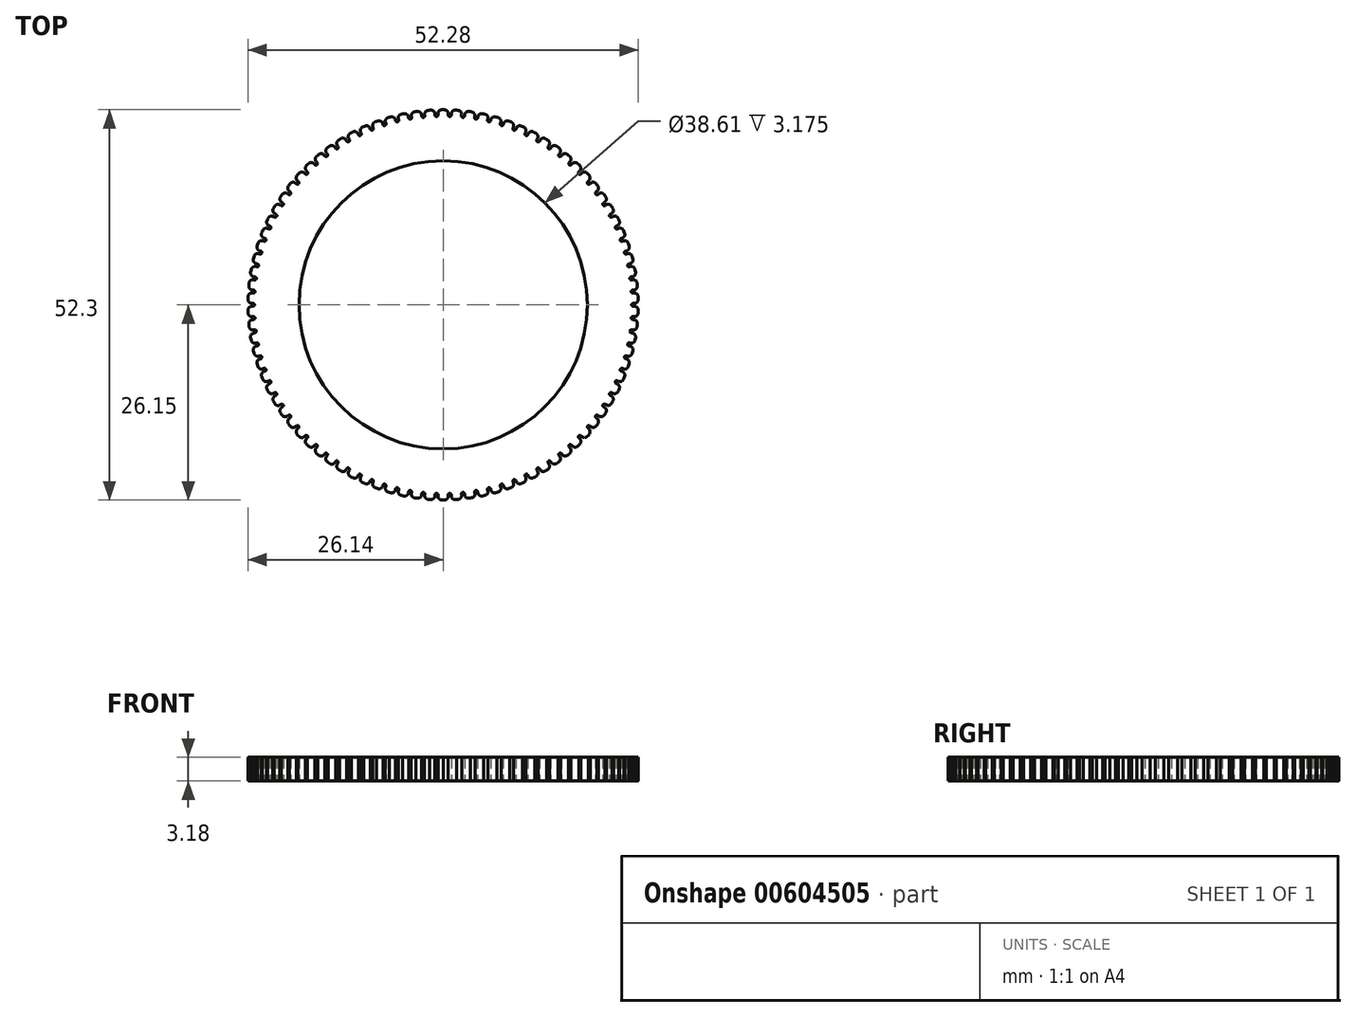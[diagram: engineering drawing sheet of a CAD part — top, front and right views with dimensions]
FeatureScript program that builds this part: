
annotation { "Feature Type Name" : "Feature", "Feature Type Description" : "" }
export const myFeature = defineFeature(function(context is Context, id is Id, definition is map)
    precondition{}
    {
        {
            var Q0;
            Q0=qCreatedBy(makeId("Top.planeOp"),FACE);
            var sketch = newSketch(context, id + "F0", { "sketchPlane" : qUnion([Q0])});
            skLineSegment(sketch, "E0", {"start": v(1.09, 25.44) * mm, "end": v(1.09, 25.44) * mm});
            skLineSegment(sketch, "E1", {"start": v(0, 0) * mm, "end": v(1.78, 25.4) * mm});
            skArc(sketch, "E2", {"start": v(0.69, 25.45) * mm, "mid": v(0.88, 25.25) * mm, "end": v(1.09, 25.44) * mm});
            skPoint(sketch, "E3.center.orphan", {"position": v(0, 25.46) * mm});
            skLineSegment(sketch, "E4", {"start": v(0.69, 25.45) * mm, "end": v(0.69, 25.45) * mm});
            skArc(sketch, "E5", {"start": v(1.82, 26.09) * mm, "mid": v(1.8, 26.09) * mm, "end": v(1.78, 26.1) * mm});
            skPoint(sketch, "E6", {"position": v(0, 26.15) * mm});
            skPoint(sketch, "E7", {"position": v(1.82, 26.09) * mm});
            skLineSegment(sketch, "E8", {"start": v(0, 26.15) * mm, "end": v(0.2, 26.15) * mm});
            skLineSegment(sketch, "E9", {"start": v(0.69, 25.45) * mm, "end": v(0.7, 25.63) * mm});
            skLineSegment(sketch, "E10", {"start": v(1.09, 25.44) * mm, "end": v(1.1, 25.6) * mm});
            skArc(sketch, "E11", {"start": v(0.7, 25.63) * mm, "mid": v(0.55, 25.99) * mm, "end": v(0.2, 26.15) * mm});
            skArc(sketch, "E12", {"start": v(1.62, 26.1) * mm, "mid": v(1.26, 25.96) * mm, "end": v(1.1, 25.6) * mm});
            skLineSegment(sketch, "E13.trimOffspring", {"start": v(1.62, 26.1) * mm, "end": v(1.82, 26.09) * mm});
            skLineSegment(sketch, "E14.1.0", {"start": v(-1.82, 26.09) * mm, "end": v(-1.62, 26.1) * mm});
            skArc(sketch, "E14.1.1", {"start": v(-1.1, 25.61) * mm, "mid": v(-1.26, 25.96) * mm, "end": v(-1.62, 26.1) * mm});
            skLineSegment(sketch, "E14.1.2", {"start": v(-1.09, 25.44) * mm, "end": v(-1.1, 25.61) * mm});
            skArc(sketch, "E14.1.3", {"start": v(-1.09, 25.44) * mm, "mid": v(-0.88, 25.25) * mm, "end": v(-0.69, 25.45) * mm});
            skLineSegment(sketch, "E14.1.4", {"start": v(-0.69, 25.45) * mm, "end": v(-0.7, 25.62) * mm});
            skArc(sketch, "E14.1.5", {"start": v(-0.2, 26.15) * mm, "mid": v(-0.56, 25.98) * mm, "end": v(-0.7, 25.62) * mm});
            skLineSegment(sketch, "E14.1.6", {"start": v(-0.2, 26.15) * mm, "end": v(0, 26.15) * mm});
            skLineSegment(sketch, "E14.2.0", {"start": v(-3.64, 25.9) * mm, "end": v(-3.44, 25.92) * mm});
            skArc(sketch, "E14.2.1", {"start": v(-2.88, 25.48) * mm, "mid": v(-3.07, 25.81) * mm, "end": v(-3.44, 25.92) * mm});
            skLineSegment(sketch, "E14.2.2", {"start": v(-2.86, 25.3) * mm, "end": v(-2.88, 25.48) * mm});
            skArc(sketch, "E14.2.3", {"start": v(-2.86, 25.3) * mm, "mid": v(-2.64, 25.13) * mm, "end": v(-2.46, 25.34) * mm});
            skLineSegment(sketch, "E14.2.4", {"start": v(-2.46, 25.34) * mm, "end": v(-2.48, 25.5) * mm});
            skArc(sketch, "E14.2.5", {"start": v(-2.03, 26.07) * mm, "mid": v(-2.37, 25.88) * mm, "end": v(-2.48, 25.5) * mm});
            skLineSegment(sketch, "E14.2.6", {"start": v(-2.03, 26.07) * mm, "end": v(-1.82, 26.09) * mm});
            skLineSegment(sketch, "E14.3.0", {"start": v(-5.44, 25.58) * mm, "end": v(-5.24, 25.62) * mm});
            skArc(sketch, "E14.3.1", {"start": v(-4.65, 25.21) * mm, "mid": v(-4.86, 25.53) * mm, "end": v(-5.24, 25.62) * mm});
            skLineSegment(sketch, "E14.3.2", {"start": v(-4.62, 25.04) * mm, "end": v(-4.65, 25.21) * mm});
            skArc(sketch, "E14.3.3", {"start": v(-4.62, 25.04) * mm, "mid": v(-4.39, 24.88) * mm, "end": v(-4.22, 25.1) * mm});
            skLineSegment(sketch, "E14.3.4", {"start": v(-4.22, 25.1) * mm, "end": v(-4.25, 25.27) * mm});
            skArc(sketch, "E14.3.5", {"start": v(-3.84, 25.86) * mm, "mid": v(-4.17, 25.65) * mm, "end": v(-4.25, 25.27) * mm});
            skLineSegment(sketch, "E14.3.6", {"start": v(-3.84, 25.86) * mm, "end": v(-3.64, 25.9) * mm});
            skLineSegment(sketch, "E14.4.0", {"start": v(-7.2, 25.14) * mm, "end": v(-7.01, 25.19) * mm});
            skArc(sketch, "E14.4.1", {"start": v(-6.4, 24.83) * mm, "mid": v(-6.63, 25.13) * mm, "end": v(-7.01, 25.19) * mm});
            skLineSegment(sketch, "E14.4.2", {"start": v(-6.35, 24.66) * mm, "end": v(-6.4, 24.83) * mm});
            skArc(sketch, "E14.4.3", {"start": v(-6.35, 24.66) * mm, "mid": v(-6.11, 24.51) * mm, "end": v(-5.97, 24.75) * mm});
            skLineSegment(sketch, "E14.4.4", {"start": v(-5.97, 24.75) * mm, "end": v(-6, 24.92) * mm});
            skArc(sketch, "E14.4.5", {"start": v(-5.64, 25.53) * mm, "mid": v(-5.95, 25.3) * mm, "end": v(-6, 24.92) * mm});
            skLineSegment(sketch, "E14.4.6", {"start": v(-5.64, 25.53) * mm, "end": v(-5.44, 25.58) * mm});
            skLineSegment(sketch, "E14.5.0", {"start": v(-8.94, 24.58) * mm, "end": v(-8.75, 24.64) * mm});
            skArc(sketch, "E14.5.1", {"start": v(-8.12, 24.32) * mm, "mid": v(-8.37, 24.6) * mm, "end": v(-8.75, 24.64) * mm});
            skLineSegment(sketch, "E14.5.2", {"start": v(-8.06, 24.15) * mm, "end": v(-8.12, 24.32) * mm});
            skArc(sketch, "E14.5.3", {"start": v(-8.06, 24.15) * mm, "mid": v(-7.8, 24.03) * mm, "end": v(-7.68, 24.28) * mm});
            skLineSegment(sketch, "E14.5.4", {"start": v(-7.68, 24.28) * mm, "end": v(-7.73, 24.44) * mm});
            skArc(sketch, "E14.5.5", {"start": v(-7.4, 25.08) * mm, "mid": v(-7.7, 24.82) * mm, "end": v(-7.73, 24.44) * mm});
            skLineSegment(sketch, "E14.5.6", {"start": v(-7.4, 25.08) * mm, "end": v(-7.2, 25.14) * mm});
            skLineSegment(sketch, "E14.6.0", {"start": v(-10.64, 23.9) * mm, "end": v(-10.45, 23.97) * mm});
            skArc(sketch, "E14.6.1", {"start": v(-9.8, 23.7) * mm, "mid": v(-10.07, 23.97) * mm, "end": v(-10.45, 23.97) * mm});
            skLineSegment(sketch, "E14.6.2", {"start": v(-9.72, 23.53) * mm, "end": v(-9.8, 23.7) * mm});
            skArc(sketch, "E14.6.3", {"start": v(-9.72, 23.53) * mm, "mid": v(-9.46, 23.42) * mm, "end": v(-9.35, 23.68) * mm});
            skLineSegment(sketch, "E14.6.4", {"start": v(-9.35, 23.68) * mm, "end": v(-9.42, 23.84) * mm});
            skArc(sketch, "E14.6.5", {"start": v(-9.13, 24.5) * mm, "mid": v(-9.41, 24.23) * mm, "end": v(-9.42, 23.84) * mm});
            skLineSegment(sketch, "E14.6.6", {"start": v(-9.13, 24.5) * mm, "end": v(-8.94, 24.58) * mm});
            skLineSegment(sketch, "E14.7.0", {"start": v(-12.28, 23.1) * mm, "end": v(-12.1, 23.18) * mm});
            skArc(sketch, "E14.7.1", {"start": v(-11.42, 22.95) * mm, "mid": v(-11.71, 23.2) * mm, "end": v(-12.1, 23.18) * mm});
            skLineSegment(sketch, "E14.7.2", {"start": v(-11.34, 22.8) * mm, "end": v(-11.42, 22.95) * mm});
            skArc(sketch, "E14.7.3", {"start": v(-11.34, 22.8) * mm, "mid": v(-11.07, 22.7) * mm, "end": v(-10.98, 22.97) * mm});
            skLineSegment(sketch, "E14.7.4", {"start": v(-10.98, 22.97) * mm, "end": v(-11.06, 23.12) * mm});
            skArc(sketch, "E14.7.5", {"start": v(-10.82, 23.8) * mm, "mid": v(-11.08, 23.51) * mm, "end": v(-11.06, 23.12) * mm});
            skLineSegment(sketch, "E14.7.6", {"start": v(-10.82, 23.8) * mm, "end": v(-10.64, 23.9) * mm});
            skLineSegment(sketch, "E14.8.0", {"start": v(-13.86, 22.18) * mm, "end": v(-13.68, 22.28) * mm});
            skArc(sketch, "E14.8.1", {"start": v(-13, 22.1) * mm, "mid": v(-13.3, 22.33) * mm, "end": v(-13.68, 22.28) * mm});
            skLineSegment(sketch, "E14.8.2", {"start": v(-12.9, 21.95) * mm, "end": v(-13, 22.1) * mm});
            skArc(sketch, "E14.8.3", {"start": v(-12.9, 21.95) * mm, "mid": v(-12.63, 21.88) * mm, "end": v(-12.56, 22.15) * mm});
            skLineSegment(sketch, "E14.8.4", {"start": v(-12.56, 22.15) * mm, "end": v(-12.64, 22.3) * mm});
            skArc(sketch, "E14.8.5", {"start": v(-12.46, 22.99) * mm, "mid": v(-12.7, 22.68) * mm, "end": v(-12.64, 22.3) * mm});
            skLineSegment(sketch, "E14.8.6", {"start": v(-12.46, 22.99) * mm, "end": v(-12.28, 23.1) * mm});
            skLineSegment(sketch, "E14.9.0", {"start": v(-15.37, 21.16) * mm, "end": v(-15.2, 21.27) * mm});
            skArc(sketch, "E14.9.1", {"start": v(-14.5, 21.14) * mm, "mid": v(-14.83, 21.35) * mm, "end": v(-15.2, 21.27) * mm});
            skLineSegment(sketch, "E14.9.2", {"start": v(-14.4, 21) * mm, "end": v(-14.5, 21.14) * mm});
            skArc(sketch, "E14.9.3", {"start": v(-14.4, 21) * mm, "mid": v(-14.13, 20.94) * mm, "end": v(-14.07, 21.22) * mm});
            skLineSegment(sketch, "E14.9.4", {"start": v(-14.07, 21.22) * mm, "end": v(-14.17, 21.36) * mm});
            skArc(sketch, "E14.9.5", {"start": v(-14.03, 22.06) * mm, "mid": v(-14.24, 21.74) * mm, "end": v(-14.17, 21.36) * mm});
            skLineSegment(sketch, "E14.9.6", {"start": v(-14.03, 22.06) * mm, "end": v(-13.86, 22.18) * mm});
            skLineSegment(sketch, "E14.10.0", {"start": v(-16.81, 20.03) * mm, "end": v(-16.65, 20.16) * mm});
            skArc(sketch, "E14.10.1", {"start": v(-15.94, 20.08) * mm, "mid": v(-16.28, 20.26) * mm, "end": v(-16.65, 20.16) * mm});
            skLineSegment(sketch, "E14.10.2", {"start": v(-15.83, 19.94) * mm, "end": v(-15.94, 20.08) * mm});
            skArc(sketch, "E14.10.3", {"start": v(-15.83, 19.94) * mm, "mid": v(-15.55, 19.9) * mm, "end": v(-15.52, 20.19) * mm});
            skLineSegment(sketch, "E14.10.4", {"start": v(-15.52, 20.19) * mm, "end": v(-15.62, 20.32) * mm});
            skArc(sketch, "E14.10.5", {"start": v(-15.53, 21.03) * mm, "mid": v(-15.72, 20.7) * mm, "end": v(-15.62, 20.32) * mm});
            skLineSegment(sketch, "E14.10.6", {"start": v(-15.53, 21.03) * mm, "end": v(-15.37, 21.16) * mm});
            skLineSegment(sketch, "E14.11.0", {"start": v(-18.17, 18.81) * mm, "end": v(-18.02, 18.95) * mm});
            skArc(sketch, "E14.11.1", {"start": v(-17.3, 18.92) * mm, "mid": v(-17.65, 19.08) * mm, "end": v(-18.02, 18.95) * mm});
            skLineSegment(sketch, "E14.11.2", {"start": v(-17.18, 18.79) * mm, "end": v(-17.3, 18.92) * mm});
            skArc(sketch, "E14.11.3", {"start": v(-17.18, 18.79) * mm, "mid": v(-16.9, 18.77) * mm, "end": v(-16.89, 19.05) * mm});
            skLineSegment(sketch, "E14.11.4", {"start": v(-16.89, 19.05) * mm, "end": v(-17, 19.18) * mm});
            skArc(sketch, "E14.11.5", {"start": v(-16.96, 19.9) * mm, "mid": v(-17.13, 19.55) * mm, "end": v(-17, 19.18) * mm});
            skLineSegment(sketch, "E14.11.6", {"start": v(-16.96, 19.9) * mm, "end": v(-16.81, 20.03) * mm});
            skLineSegment(sketch, "E14.12.0", {"start": v(-19.43, 17.5) * mm, "end": v(-19.3, 17.64) * mm});
            skArc(sketch, "E14.12.1", {"start": v(-18.58, 17.66) * mm, "mid": v(-18.94, 17.8) * mm, "end": v(-19.3, 17.64) * mm});
            skLineSegment(sketch, "E14.12.2", {"start": v(-18.45, 17.54) * mm, "end": v(-18.58, 17.66) * mm});
            skArc(sketch, "E14.12.3", {"start": v(-18.45, 17.54) * mm, "mid": v(-18.17, 17.55) * mm, "end": v(-18.18, 17.83) * mm});
            skLineSegment(sketch, "E14.12.4", {"start": v(-18.18, 17.83) * mm, "end": v(-18.3, 17.95) * mm});
            skArc(sketch, "E14.12.5", {"start": v(-18.3, 18.67) * mm, "mid": v(-18.45, 18.3) * mm, "end": v(-18.3, 17.95) * mm});
            skLineSegment(sketch, "E14.12.6", {"start": v(-18.3, 18.67) * mm, "end": v(-18.17, 18.81) * mm});
            skLineSegment(sketch, "E14.13.0", {"start": v(-20.6, 16.1) * mm, "end": v(-20.48, 16.26) * mm});
            skArc(sketch, "E14.13.1", {"start": v(-19.77, 16.32) * mm, "mid": v(-20.14, 16.43) * mm, "end": v(-20.48, 16.26) * mm});
            skLineSegment(sketch, "E14.13.2", {"start": v(-19.63, 16.21) * mm, "end": v(-19.77, 16.32) * mm});
            skArc(sketch, "E14.13.3", {"start": v(-19.63, 16.21) * mm, "mid": v(-19.35, 16.24) * mm, "end": v(-19.37, 16.52) * mm});
            skLineSegment(sketch, "E14.13.4", {"start": v(-19.37, 16.52) * mm, "end": v(-19.5, 16.63) * mm});
            skArc(sketch, "E14.13.5", {"start": v(-19.57, 17.34) * mm, "mid": v(-19.68, 16.97) * mm, "end": v(-19.5, 16.63) * mm});
            skLineSegment(sketch, "E14.13.6", {"start": v(-19.57, 17.34) * mm, "end": v(-19.43, 17.5) * mm});
            skLineSegment(sketch, "E14.14.0", {"start": v(-21.68, 14.62) * mm, "end": v(-21.56, 14.79) * mm});
            skArc(sketch, "E14.14.1", {"start": v(-20.86, 14.9) * mm, "mid": v(-21.24, 14.99) * mm, "end": v(-21.56, 14.79) * mm});
            skLineSegment(sketch, "E14.14.2", {"start": v(-20.72, 14.8) * mm, "end": v(-20.86, 14.9) * mm});
            skArc(sketch, "E14.14.3", {"start": v(-20.72, 14.8) * mm, "mid": v(-20.44, 14.85) * mm, "end": v(-20.48, 15.13) * mm});
            skLineSegment(sketch, "E14.14.4", {"start": v(-20.48, 15.13) * mm, "end": v(-20.62, 15.23) * mm});
            skArc(sketch, "E14.14.5", {"start": v(-20.73, 15.94) * mm, "mid": v(-20.82, 15.56) * mm, "end": v(-20.62, 15.23) * mm});
            skLineSegment(sketch, "E14.14.6", {"start": v(-20.73, 15.94) * mm, "end": v(-20.6, 16.1) * mm});
            skLineSegment(sketch, "E14.15.0", {"start": v(-22.65, 13.08) * mm, "end": v(-22.54, 13.25) * mm});
            skArc(sketch, "E14.15.1", {"start": v(-21.85, 13.41) * mm, "mid": v(-22.23, 13.47) * mm, "end": v(-22.54, 13.25) * mm});
            skLineSegment(sketch, "E14.15.2", {"start": v(-21.7, 13.32) * mm, "end": v(-21.85, 13.41) * mm});
            skArc(sketch, "E14.15.3", {"start": v(-21.7, 13.32) * mm, "mid": v(-21.42, 13.39) * mm, "end": v(-21.49, 13.66) * mm});
            skLineSegment(sketch, "E14.15.4", {"start": v(-21.49, 13.66) * mm, "end": v(-21.63, 13.75) * mm});
            skArc(sketch, "E14.15.5", {"start": v(-21.79, 14.45) * mm, "mid": v(-21.85, 14.07) * mm, "end": v(-21.63, 13.75) * mm});
            skLineSegment(sketch, "E14.15.6", {"start": v(-21.79, 14.45) * mm, "end": v(-21.68, 14.62) * mm});
            skLineSegment(sketch, "E14.16.0", {"start": v(-23.5, 11.46) * mm, "end": v(-23.41, 11.64) * mm});
            skArc(sketch, "E14.16.1", {"start": v(-22.73, 11.86) * mm, "mid": v(-23.12, 11.89) * mm, "end": v(-23.41, 11.64) * mm});
            skLineSegment(sketch, "E14.16.2", {"start": v(-22.57, 11.78) * mm, "end": v(-22.73, 11.86) * mm});
            skArc(sketch, "E14.16.3", {"start": v(-22.57, 11.78) * mm, "mid": v(-22.3, 11.86) * mm, "end": v(-22.39, 12.13) * mm});
            skLineSegment(sketch, "E14.16.4", {"start": v(-22.39, 12.13) * mm, "end": v(-22.53, 12.2) * mm});
            skArc(sketch, "E14.16.5", {"start": v(-22.74, 12.9) * mm, "mid": v(-22.78, 12.5) * mm, "end": v(-22.53, 12.2) * mm});
            skLineSegment(sketch, "E14.16.6", {"start": v(-22.74, 12.9) * mm, "end": v(-22.65, 13.08) * mm});
            skLineSegment(sketch, "E14.17.0", {"start": v(-24.25, 9.8) * mm, "end": v(-24.17, 9.98) * mm});
            skArc(sketch, "E14.17.1", {"start": v(-23.5, 10.24) * mm, "mid": v(-23.89, 10.25) * mm, "end": v(-24.17, 9.98) * mm});
            skLineSegment(sketch, "E14.17.2", {"start": v(-23.34, 10.17) * mm, "end": v(-23.5, 10.24) * mm});
            skArc(sketch, "E14.17.3", {"start": v(-23.34, 10.17) * mm, "mid": v(-23.08, 10.28) * mm, "end": v(-23.18, 10.54) * mm});
            skLineSegment(sketch, "E14.17.4", {"start": v(-23.18, 10.54) * mm, "end": v(-23.33, 10.6) * mm});
            skArc(sketch, "E14.17.5", {"start": v(-23.59, 11.28) * mm, "mid": v(-23.6, 10.89) * mm, "end": v(-23.33, 10.6) * mm});
            skLineSegment(sketch, "E14.17.6", {"start": v(-23.59, 11.28) * mm, "end": v(-23.5, 11.46) * mm});
            skLineSegment(sketch, "E14.18.0", {"start": v(-24.87, 8.08) * mm, "end": v(-24.8, 8.27) * mm});
            skArc(sketch, "E14.18.1", {"start": v(-24.16, 8.58) * mm, "mid": v(-24.54, 8.56) * mm, "end": v(-24.8, 8.27) * mm});
            skLineSegment(sketch, "E14.18.2", {"start": v(-24, 8.52) * mm, "end": v(-24.16, 8.58) * mm});
            skArc(sketch, "E14.18.3", {"start": v(-24, 8.52) * mm, "mid": v(-23.74, 8.64) * mm, "end": v(-23.86, 8.9) * mm});
            skLineSegment(sketch, "E14.18.4", {"start": v(-23.86, 8.9) * mm, "end": v(-24.01, 8.95) * mm});
            skArc(sketch, "E14.18.5", {"start": v(-24.32, 9.6) * mm, "mid": v(-24.3, 9.22) * mm, "end": v(-24.01, 8.95) * mm});
            skLineSegment(sketch, "E14.18.6", {"start": v(-24.32, 9.6) * mm, "end": v(-24.25, 9.8) * mm});
            skLineSegment(sketch, "E14.19.0", {"start": v(-25.38, 6.33) * mm, "end": v(-25.32, 6.52) * mm});
            skArc(sketch, "E14.19.1", {"start": v(-24.7, 6.87) * mm, "mid": v(-25.08, 6.82) * mm, "end": v(-25.32, 6.52) * mm});
            skLineSegment(sketch, "E14.19.2", {"start": v(-24.53, 6.83) * mm, "end": v(-24.7, 6.87) * mm});
            skArc(sketch, "E14.19.3", {"start": v(-24.53, 6.83) * mm, "mid": v(-24.28, 6.96) * mm, "end": v(-24.42, 7.2) * mm});
            skLineSegment(sketch, "E14.19.4", {"start": v(-24.42, 7.2) * mm, "end": v(-24.58, 7.26) * mm});
            skArc(sketch, "E14.19.5", {"start": v(-24.93, 7.88) * mm, "mid": v(-24.88, 7.5) * mm, "end": v(-24.58, 7.26) * mm});
            skLineSegment(sketch, "E14.19.6", {"start": v(-24.93, 7.88) * mm, "end": v(-24.87, 8.08) * mm});
            skLineSegment(sketch, "E14.20.0", {"start": v(-25.75, 4.54) * mm, "end": v(-25.71, 4.74) * mm});
            skArc(sketch, "E14.20.1", {"start": v(-25.12, 5.13) * mm, "mid": v(-25.5, 5.06) * mm, "end": v(-25.71, 4.74) * mm});
            skLineSegment(sketch, "E14.20.2", {"start": v(-24.95, 5.1) * mm, "end": v(-25.12, 5.13) * mm});
            skArc(sketch, "E14.20.3", {"start": v(-24.95, 5.1) * mm, "mid": v(-24.71, 5.25) * mm, "end": v(-24.86, 5.49) * mm});
            skLineSegment(sketch, "E14.20.4", {"start": v(-24.86, 5.49) * mm, "end": v(-25.03, 5.52) * mm});
            skArc(sketch, "E14.20.5", {"start": v(-25.42, 6.13) * mm, "mid": v(-25.35, 5.74) * mm, "end": v(-25.03, 5.52) * mm});
            skLineSegment(sketch, "E14.20.6", {"start": v(-25.42, 6.13) * mm, "end": v(-25.38, 6.33) * mm});
            skLineSegment(sketch, "E14.21.0", {"start": v(-26, 2.73) * mm, "end": v(-25.98, 2.93) * mm});
            skArc(sketch, "E14.21.1", {"start": v(-25.42, 3.37) * mm, "mid": v(-25.79, 3.27) * mm, "end": v(-25.98, 2.93) * mm});
            skLineSegment(sketch, "E14.21.2", {"start": v(-25.24, 3.35) * mm, "end": v(-25.42, 3.37) * mm});
            skArc(sketch, "E14.21.3", {"start": v(-25.24, 3.35) * mm, "mid": v(-25.02, 3.52) * mm, "end": v(-25.18, 3.74) * mm});
            skLineSegment(sketch, "E14.21.4", {"start": v(-25.18, 3.74) * mm, "end": v(-25.35, 3.76) * mm});
            skArc(sketch, "E14.21.5", {"start": v(-25.78, 4.34) * mm, "mid": v(-25.69, 3.96) * mm, "end": v(-25.35, 3.76) * mm});
            skLineSegment(sketch, "E14.21.6", {"start": v(-25.78, 4.34) * mm, "end": v(-25.75, 4.54) * mm});
            skLineSegment(sketch, "E14.22.0", {"start": v(-26.14, 0.91) * mm, "end": v(-26.12, 1.11) * mm});
            skArc(sketch, "E14.22.1", {"start": v(-25.59, 1.59) * mm, "mid": v(-25.95, 1.46) * mm, "end": v(-26.12, 1.11) * mm});
            skLineSegment(sketch, "E14.22.2", {"start": v(-25.41, 1.58) * mm, "end": v(-25.59, 1.59) * mm});
            skArc(sketch, "E14.22.3", {"start": v(-25.41, 1.58) * mm, "mid": v(-25.2, 1.76) * mm, "end": v(-25.38, 1.98) * mm});
            skLineSegment(sketch, "E14.22.4", {"start": v(-25.38, 1.98) * mm, "end": v(-25.55, 1.99) * mm});
            skArc(sketch, "E14.22.5", {"start": v(-26.02, 2.53) * mm, "mid": v(-25.9, 2.16) * mm, "end": v(-25.55, 1.99) * mm});
            skLineSegment(sketch, "E14.22.6", {"start": v(-26.02, 2.53) * mm, "end": v(-26, 2.73) * mm});
            skLineSegment(sketch, "E14.23.0", {"start": v(-26.14, -0.91) * mm, "end": v(-26.14, -0.71) * mm});
            skArc(sketch, "E14.23.1", {"start": v(-25.64, -0.2) * mm, "mid": v(-26, -0.35) * mm, "end": v(-26.14, -0.71) * mm});
            skLineSegment(sketch, "E14.23.2", {"start": v(-25.46, -0.2) * mm, "end": v(-25.64, -0.2) * mm});
            skArc(sketch, "E14.23.3", {"start": v(-25.46, -0.2) * mm, "mid": v(-25.26, 0) * mm, "end": v(-25.46, 0.2) * mm});
            skLineSegment(sketch, "E14.23.4", {"start": v(-25.46, 0.2) * mm, "end": v(-25.63, 0.2) * mm});
            skArc(sketch, "E14.23.5", {"start": v(-26.14, 0.7) * mm, "mid": v(-25.99, 0.35) * mm, "end": v(-25.63, 0.2) * mm});
            skLineSegment(sketch, "E14.23.6", {"start": v(-26.14, 0.7) * mm, "end": v(-26.14, 0.91) * mm});
            skLineSegment(sketch, "E14.24.0", {"start": v(-26, -2.73) * mm, "end": v(-26.02, -2.53) * mm});
            skArc(sketch, "E14.24.1", {"start": v(-25.56, -2) * mm, "mid": v(-25.9, -2.17) * mm, "end": v(-26.02, -2.53) * mm});
            skLineSegment(sketch, "E14.24.2", {"start": v(-25.38, -1.98) * mm, "end": v(-25.56, -2) * mm});
            skArc(sketch, "E14.24.3", {"start": v(-25.38, -1.98) * mm, "mid": v(-25.2, -1.76) * mm, "end": v(-25.41, -1.58) * mm});
            skLineSegment(sketch, "E14.24.4", {"start": v(-25.41, -1.58) * mm, "end": v(-25.58, -1.59) * mm});
            skArc(sketch, "E14.24.5", {"start": v(-26.12, -1.12) * mm, "mid": v(-25.95, -1.46) * mm, "end": v(-25.58, -1.59) * mm});
            skLineSegment(sketch, "E14.24.6", {"start": v(-26.12, -1.12) * mm, "end": v(-26.14, -0.91) * mm});
            skLineSegment(sketch, "E14.25.0", {"start": v(-25.75, -4.54) * mm, "end": v(-25.78, -4.34) * mm});
            skArc(sketch, "E14.25.1", {"start": v(-25.36, -3.77) * mm, "mid": v(-25.69, -3.97) * mm, "end": v(-25.78, -4.34) * mm});
            skLineSegment(sketch, "E14.25.2", {"start": v(-25.18, -3.74) * mm, "end": v(-25.36, -3.77) * mm});
            skArc(sketch, "E14.25.3", {"start": v(-25.18, -3.74) * mm, "mid": v(-25.02, -3.52) * mm, "end": v(-25.24, -3.35) * mm});
            skLineSegment(sketch, "E14.25.4", {"start": v(-25.24, -3.35) * mm, "end": v(-25.4, -3.37) * mm});
            skArc(sketch, "E14.25.5", {"start": v(-25.98, -2.94) * mm, "mid": v(-25.78, -3.27) * mm, "end": v(-25.4, -3.37) * mm});
            skLineSegment(sketch, "E14.25.6", {"start": v(-25.98, -2.94) * mm, "end": v(-26, -2.73) * mm});
            skLineSegment(sketch, "E14.26.0", {"start": v(-25.38, -6.33) * mm, "end": v(-25.42, -6.13) * mm});
            skArc(sketch, "E14.26.1", {"start": v(-25.03, -5.53) * mm, "mid": v(-25.35, -5.75) * mm, "end": v(-25.42, -6.13) * mm});
            skLineSegment(sketch, "E14.26.2", {"start": v(-24.86, -5.49) * mm, "end": v(-25.03, -5.53) * mm});
            skArc(sketch, "E14.26.3", {"start": v(-24.86, -5.49) * mm, "mid": v(-24.71, -5.25) * mm, "end": v(-24.95, -5.1) * mm});
            skLineSegment(sketch, "E14.26.4", {"start": v(-24.95, -5.1) * mm, "end": v(-25.1, -5.13) * mm});
            skArc(sketch, "E14.26.5", {"start": v(-25.71, -4.74) * mm, "mid": v(-25.5, -5.06) * mm, "end": v(-25.1, -5.13) * mm});
            skLineSegment(sketch, "E14.26.6", {"start": v(-25.71, -4.74) * mm, "end": v(-25.75, -4.54) * mm});
            skLineSegment(sketch, "E14.27.0", {"start": v(-24.87, -8.08) * mm, "end": v(-24.93, -7.89) * mm});
            skArc(sketch, "E14.27.1", {"start": v(-24.59, -7.26) * mm, "mid": v(-24.89, -7.5) * mm, "end": v(-24.93, -7.89) * mm});
            skLineSegment(sketch, "E14.27.2", {"start": v(-24.42, -7.2) * mm, "end": v(-24.59, -7.26) * mm});
            skArc(sketch, "E14.27.3", {"start": v(-24.42, -7.2) * mm, "mid": v(-24.28, -6.96) * mm, "end": v(-24.53, -6.83) * mm});
            skLineSegment(sketch, "E14.27.4", {"start": v(-24.53, -6.83) * mm, "end": v(-24.7, -6.87) * mm});
            skArc(sketch, "E14.27.5", {"start": v(-25.32, -6.52) * mm, "mid": v(-25.08, -6.83) * mm, "end": v(-24.7, -6.87) * mm});
            skLineSegment(sketch, "E14.27.6", {"start": v(-25.32, -6.52) * mm, "end": v(-25.38, -6.33) * mm});
            skLineSegment(sketch, "E14.28.0", {"start": v(-24.25, -9.8) * mm, "end": v(-24.32, -9.6) * mm});
            skArc(sketch, "E14.28.1", {"start": v(-24.02, -8.96) * mm, "mid": v(-24.3, -9.22) * mm, "end": v(-24.32, -9.6) * mm});
            skLineSegment(sketch, "E14.28.2", {"start": v(-23.86, -8.9) * mm, "end": v(-24.02, -8.96) * mm});
            skArc(sketch, "E14.28.3", {"start": v(-23.86, -8.9) * mm, "mid": v(-23.74, -8.64) * mm, "end": v(-24, -8.52) * mm});
            skLineSegment(sketch, "E14.28.4", {"start": v(-24, -8.52) * mm, "end": v(-24.15, -8.58) * mm});
            skArc(sketch, "E14.28.5", {"start": v(-24.8, -8.27) * mm, "mid": v(-24.54, -8.56) * mm, "end": v(-24.15, -8.58) * mm});
            skLineSegment(sketch, "E14.28.6", {"start": v(-24.8, -8.27) * mm, "end": v(-24.87, -8.08) * mm});
            skLineSegment(sketch, "E14.29.0", {"start": v(-23.5, -11.46) * mm, "end": v(-23.59, -11.28) * mm});
            skArc(sketch, "E14.29.1", {"start": v(-23.34, -10.61) * mm, "mid": v(-23.6, -10.9) * mm, "end": v(-23.59, -11.28) * mm});
            skLineSegment(sketch, "E14.29.2", {"start": v(-23.18, -10.54) * mm, "end": v(-23.34, -10.61) * mm});
            skArc(sketch, "E14.29.3", {"start": v(-23.18, -10.54) * mm, "mid": v(-23.08, -10.28) * mm, "end": v(-23.34, -10.17) * mm});
            skLineSegment(sketch, "E14.29.4", {"start": v(-23.34, -10.17) * mm, "end": v(-23.5, -10.24) * mm});
            skArc(sketch, "E14.29.5", {"start": v(-24.16, -9.98) * mm, "mid": v(-23.88, -10.25) * mm, "end": v(-23.5, -10.24) * mm});
            skLineSegment(sketch, "E14.29.6", {"start": v(-24.16, -9.98) * mm, "end": v(-24.25, -9.8) * mm});
            skLineSegment(sketch, "E14.30.0", {"start": v(-22.65, -13.08) * mm, "end": v(-22.74, -12.9) * mm});
            skArc(sketch, "E14.30.1", {"start": v(-22.54, -12.22) * mm, "mid": v(-22.78, -12.52) * mm, "end": v(-22.74, -12.9) * mm});
            skLineSegment(sketch, "E14.30.2", {"start": v(-22.39, -12.13) * mm, "end": v(-22.54, -12.22) * mm});
            skArc(sketch, "E14.30.3", {"start": v(-22.39, -12.13) * mm, "mid": v(-22.3, -11.86) * mm, "end": v(-22.57, -11.78) * mm});
            skLineSegment(sketch, "E14.30.4", {"start": v(-22.57, -11.78) * mm, "end": v(-22.72, -11.86) * mm});
            skArc(sketch, "E14.30.5", {"start": v(-23.4, -11.65) * mm, "mid": v(-23.1, -11.9) * mm, "end": v(-22.72, -11.86) * mm});
            skLineSegment(sketch, "E14.30.6", {"start": v(-23.4, -11.65) * mm, "end": v(-23.5, -11.46) * mm});
            skLineSegment(sketch, "E14.31.0", {"start": v(-21.68, -14.62) * mm, "end": v(-21.79, -14.45) * mm});
            skArc(sketch, "E14.31.1", {"start": v(-21.63, -13.76) * mm, "mid": v(-21.85, -14.07) * mm, "end": v(-21.79, -14.45) * mm});
            skLineSegment(sketch, "E14.31.2", {"start": v(-21.49, -13.66) * mm, "end": v(-21.63, -13.76) * mm});
            skArc(sketch, "E14.31.3", {"start": v(-21.49, -13.66) * mm, "mid": v(-21.42, -13.39) * mm, "end": v(-21.7, -13.32) * mm});
            skLineSegment(sketch, "E14.31.4", {"start": v(-21.7, -13.32) * mm, "end": v(-21.84, -13.41) * mm});
            skArc(sketch, "E14.31.5", {"start": v(-22.54, -13.25) * mm, "mid": v(-22.22, -13.48) * mm, "end": v(-21.84, -13.41) * mm});
            skLineSegment(sketch, "E14.31.6", {"start": v(-22.54, -13.25) * mm, "end": v(-22.65, -13.08) * mm});
            skLineSegment(sketch, "E14.32.0", {"start": v(-20.6, -16.1) * mm, "end": v(-20.73, -15.94) * mm});
            skArc(sketch, "E14.32.1", {"start": v(-20.62, -15.23) * mm, "mid": v(-20.82, -15.56) * mm, "end": v(-20.73, -15.94) * mm});
            skLineSegment(sketch, "E14.32.2", {"start": v(-20.48, -15.13) * mm, "end": v(-20.62, -15.23) * mm});
            skArc(sketch, "E14.32.3", {"start": v(-20.48, -15.13) * mm, "mid": v(-20.44, -14.85) * mm, "end": v(-20.72, -14.8) * mm});
            skLineSegment(sketch, "E14.32.4", {"start": v(-20.72, -14.8) * mm, "end": v(-20.85, -14.9) * mm});
            skArc(sketch, "E14.32.5", {"start": v(-21.56, -14.79) * mm, "mid": v(-21.23, -15) * mm, "end": v(-20.85, -14.9) * mm});
            skLineSegment(sketch, "E14.32.6", {"start": v(-21.56, -14.79) * mm, "end": v(-21.68, -14.62) * mm});
            skLineSegment(sketch, "E14.33.0", {"start": v(-19.43, -17.5) * mm, "end": v(-19.56, -17.34) * mm});
            skArc(sketch, "E14.33.1", {"start": v(-19.5, -16.63) * mm, "mid": v(-19.68, -16.98) * mm, "end": v(-19.56, -17.34) * mm});
            skLineSegment(sketch, "E14.33.2", {"start": v(-19.37, -16.52) * mm, "end": v(-19.5, -16.63) * mm});
            skArc(sketch, "E14.33.3", {"start": v(-19.37, -16.52) * mm, "mid": v(-19.35, -16.24) * mm, "end": v(-19.63, -16.21) * mm});
            skLineSegment(sketch, "E14.33.4", {"start": v(-19.63, -16.21) * mm, "end": v(-19.76, -16.32) * mm});
            skArc(sketch, "E14.33.5", {"start": v(-20.48, -16.26) * mm, "mid": v(-20.13, -16.44) * mm, "end": v(-19.76, -16.32) * mm});
            skLineSegment(sketch, "E14.33.6", {"start": v(-20.48, -16.26) * mm, "end": v(-20.6, -16.1) * mm});
            skLineSegment(sketch, "E14.34.0", {"start": v(-18.17, -18.81) * mm, "end": v(-18.3, -18.67) * mm});
            skArc(sketch, "E14.34.1", {"start": v(-18.3, -17.96) * mm, "mid": v(-18.45, -18.3) * mm, "end": v(-18.3, -18.67) * mm});
            skLineSegment(sketch, "E14.34.2", {"start": v(-18.18, -17.83) * mm, "end": v(-18.3, -17.96) * mm});
            skArc(sketch, "E14.34.3", {"start": v(-18.18, -17.83) * mm, "mid": v(-18.17, -17.55) * mm, "end": v(-18.45, -17.54) * mm});
            skLineSegment(sketch, "E14.34.4", {"start": v(-18.45, -17.54) * mm, "end": v(-18.57, -17.66) * mm});
            skArc(sketch, "E14.34.5", {"start": v(-19.3, -17.65) * mm, "mid": v(-18.94, -17.8) * mm, "end": v(-18.57, -17.66) * mm});
            skLineSegment(sketch, "E14.34.6", {"start": v(-19.3, -17.65) * mm, "end": v(-19.43, -17.5) * mm});
            skLineSegment(sketch, "E14.35.0", {"start": v(-16.81, -20.03) * mm, "end": v(-16.96, -19.9) * mm});
            skArc(sketch, "E14.35.1", {"start": v(-17, -19.19) * mm, "mid": v(-17.13, -19.55) * mm, "end": v(-16.96, -19.9) * mm});
            skLineSegment(sketch, "E14.35.2", {"start": v(-16.89, -19.05) * mm, "end": v(-17, -19.19) * mm});
            skArc(sketch, "E14.35.3", {"start": v(-16.89, -19.05) * mm, "mid": v(-16.9, -18.77) * mm, "end": v(-17.18, -18.79) * mm});
            skLineSegment(sketch, "E14.35.4", {"start": v(-17.18, -18.79) * mm, "end": v(-17.3, -18.91) * mm});
            skArc(sketch, "E14.35.5", {"start": v(-18.01, -18.95) * mm, "mid": v(-17.65, -19.08) * mm, "end": v(-17.3, -18.91) * mm});
            skLineSegment(sketch, "E14.35.6", {"start": v(-18.01, -18.95) * mm, "end": v(-18.17, -18.81) * mm});
            skLineSegment(sketch, "E14.36.0", {"start": v(-15.37, -21.16) * mm, "end": v(-15.53, -21.03) * mm});
            skArc(sketch, "E14.36.1", {"start": v(-15.62, -20.33) * mm, "mid": v(-15.72, -20.7) * mm, "end": v(-15.53, -21.03) * mm});
            skLineSegment(sketch, "E14.36.2", {"start": v(-15.52, -20.19) * mm, "end": v(-15.62, -20.33) * mm});
            skArc(sketch, "E14.36.3", {"start": v(-15.52, -20.19) * mm, "mid": v(-15.55, -19.9) * mm, "end": v(-15.83, -19.94) * mm});
            skLineSegment(sketch, "E14.36.4", {"start": v(-15.83, -19.94) * mm, "end": v(-15.94, -20.07) * mm});
            skArc(sketch, "E14.36.5", {"start": v(-16.65, -20.16) * mm, "mid": v(-16.27, -20.26) * mm, "end": v(-15.94, -20.07) * mm});
            skLineSegment(sketch, "E14.36.6", {"start": v(-16.65, -20.16) * mm, "end": v(-16.81, -20.03) * mm});
            skLineSegment(sketch, "E14.37.0", {"start": v(-13.86, -22.18) * mm, "end": v(-14.03, -22.07) * mm});
            skArc(sketch, "E14.37.1", {"start": v(-14.17, -21.37) * mm, "mid": v(-14.24, -21.75) * mm, "end": v(-14.03, -22.07) * mm});
            skLineSegment(sketch, "E14.37.2", {"start": v(-14.07, -21.22) * mm, "end": v(-14.17, -21.37) * mm});
            skArc(sketch, "E14.37.3", {"start": v(-14.07, -21.22) * mm, "mid": v(-14.13, -20.94) * mm, "end": v(-14.4, -21) * mm});
            skLineSegment(sketch, "E14.37.4", {"start": v(-14.4, -21) * mm, "end": v(-14.5, -21.14) * mm});
            skArc(sketch, "E14.37.5", {"start": v(-15.2, -21.27) * mm, "mid": v(-14.82, -21.35) * mm, "end": v(-14.5, -21.14) * mm});
            skLineSegment(sketch, "E14.37.6", {"start": v(-15.2, -21.27) * mm, "end": v(-15.37, -21.16) * mm});
            skLineSegment(sketch, "E14.38.0", {"start": v(-12.28, -23.1) * mm, "end": v(-12.45, -23) * mm});
            skArc(sketch, "E14.38.1", {"start": v(-12.64, -22.3) * mm, "mid": v(-12.69, -22.69) * mm, "end": v(-12.45, -23) * mm});
            skLineSegment(sketch, "E14.38.2", {"start": v(-12.56, -22.15) * mm, "end": v(-12.64, -22.3) * mm});
            skArc(sketch, "E14.38.3", {"start": v(-12.56, -22.15) * mm, "mid": v(-12.63, -21.88) * mm, "end": v(-12.9, -21.95) * mm});
            skLineSegment(sketch, "E14.38.4", {"start": v(-12.9, -21.95) * mm, "end": v(-12.99, -22.1) * mm});
            skArc(sketch, "E14.38.5", {"start": v(-13.68, -22.28) * mm, "mid": v(-13.3, -22.33) * mm, "end": v(-12.99, -22.1) * mm});
            skLineSegment(sketch, "E14.38.6", {"start": v(-13.68, -22.28) * mm, "end": v(-13.86, -22.18) * mm});
            skLineSegment(sketch, "E14.39.0", {"start": v(-10.64, -23.9) * mm, "end": v(-10.82, -23.8) * mm});
            skArc(sketch, "E14.39.1", {"start": v(-11.06, -23.13) * mm, "mid": v(-11.07, -23.52) * mm, "end": v(-10.82, -23.8) * mm});
            skLineSegment(sketch, "E14.39.2", {"start": v(-10.98, -22.97) * mm, "end": v(-11.06, -23.13) * mm});
            skArc(sketch, "E14.39.3", {"start": v(-10.98, -22.97) * mm, "mid": v(-11.07, -22.7) * mm, "end": v(-11.34, -22.8) * mm});
            skLineSegment(sketch, "E14.39.4", {"start": v(-11.34, -22.8) * mm, "end": v(-11.41, -22.95) * mm});
            skArc(sketch, "E14.39.5", {"start": v(-12.1, -23.18) * mm, "mid": v(-11.7, -23.2) * mm, "end": v(-11.41, -22.95) * mm});
            skLineSegment(sketch, "E14.39.6", {"start": v(-12.1, -23.18) * mm, "end": v(-12.28, -23.1) * mm});
            skLineSegment(sketch, "E14.40.0", {"start": v(-8.94, -24.58) * mm, "end": v(-9.13, -24.5) * mm});
            skArc(sketch, "E14.40.1", {"start": v(-9.42, -23.85) * mm, "mid": v(-9.4, -24.23) * mm, "end": v(-9.13, -24.5) * mm});
            skLineSegment(sketch, "E14.40.2", {"start": v(-9.35, -23.68) * mm, "end": v(-9.42, -23.85) * mm});
            skArc(sketch, "E14.40.3", {"start": v(-9.35, -23.68) * mm, "mid": v(-9.46, -23.42) * mm, "end": v(-9.72, -23.53) * mm});
            skLineSegment(sketch, "E14.40.4", {"start": v(-9.72, -23.53) * mm, "end": v(-9.79, -23.69) * mm});
            skArc(sketch, "E14.40.5", {"start": v(-10.45, -23.97) * mm, "mid": v(-10.06, -23.96) * mm, "end": v(-9.79, -23.69) * mm});
            skLineSegment(sketch, "E14.40.6", {"start": v(-10.45, -23.97) * mm, "end": v(-10.64, -23.9) * mm});
            skLineSegment(sketch, "E14.41.0", {"start": v(-7.2, -25.14) * mm, "end": v(-7.4, -25.08) * mm});
            skArc(sketch, "E14.41.1", {"start": v(-7.73, -24.45) * mm, "mid": v(-7.7, -24.83) * mm, "end": v(-7.4, -25.08) * mm});
            skLineSegment(sketch, "E14.41.2", {"start": v(-7.68, -24.28) * mm, "end": v(-7.73, -24.45) * mm});
            skArc(sketch, "E14.41.3", {"start": v(-7.68, -24.28) * mm, "mid": v(-7.8, -24.03) * mm, "end": v(-8.06, -24.15) * mm});
            skLineSegment(sketch, "E14.41.4", {"start": v(-8.06, -24.15) * mm, "end": v(-8.1, -24.31) * mm});
            skArc(sketch, "E14.41.5", {"start": v(-8.75, -24.64) * mm, "mid": v(-8.36, -24.6) * mm, "end": v(-8.1, -24.31) * mm});
            skLineSegment(sketch, "E14.41.6", {"start": v(-8.75, -24.64) * mm, "end": v(-8.94, -24.58) * mm});
            skLineSegment(sketch, "E14.42.0", {"start": v(-5.44, -25.58) * mm, "end": v(-5.63, -25.53) * mm});
            skArc(sketch, "E14.42.1", {"start": v(-6, -24.92) * mm, "mid": v(-5.94, -25.3) * mm, "end": v(-5.63, -25.53) * mm});
            skLineSegment(sketch, "E14.42.2", {"start": v(-5.97, -24.75) * mm, "end": v(-6, -24.92) * mm});
            skArc(sketch, "E14.42.3", {"start": v(-5.97, -24.75) * mm, "mid": v(-6.11, -24.51) * mm, "end": v(-6.35, -24.66) * mm});
            skLineSegment(sketch, "E14.42.4", {"start": v(-6.35, -24.66) * mm, "end": v(-6.4, -24.82) * mm});
            skArc(sketch, "E14.42.5", {"start": v(-7, -25.19) * mm, "mid": v(-6.63, -25.13) * mm, "end": v(-6.4, -24.82) * mm});
            skLineSegment(sketch, "E14.42.6", {"start": v(-7, -25.19) * mm, "end": v(-7.2, -25.14) * mm});
            skLineSegment(sketch, "E14.43.0", {"start": v(-3.64, -25.9) * mm, "end": v(-3.84, -25.86) * mm});
            skArc(sketch, "E14.43.1", {"start": v(-4.25, -25.28) * mm, "mid": v(-4.16, -25.66) * mm, "end": v(-3.84, -25.86) * mm});
            skLineSegment(sketch, "E14.43.2", {"start": v(-4.22, -25.1) * mm, "end": v(-4.25, -25.28) * mm});
            skArc(sketch, "E14.43.3", {"start": v(-4.22, -25.1) * mm, "mid": v(-4.39, -24.88) * mm, "end": v(-4.62, -25.04) * mm});
            skLineSegment(sketch, "E14.43.4", {"start": v(-4.62, -25.04) * mm, "end": v(-4.65, -25.2) * mm});
            skArc(sketch, "E14.43.5", {"start": v(-5.24, -25.62) * mm, "mid": v(-4.86, -25.53) * mm, "end": v(-4.65, -25.2) * mm});
            skLineSegment(sketch, "E14.43.6", {"start": v(-5.24, -25.62) * mm, "end": v(-5.44, -25.58) * mm});
            skLineSegment(sketch, "E14.44.0", {"start": v(-1.82, -26.09) * mm, "end": v(-2.02, -26.07) * mm});
            skArc(sketch, "E14.44.1", {"start": v(-2.48, -25.52) * mm, "mid": v(-2.36, -25.89) * mm, "end": v(-2.02, -26.07) * mm});
            skLineSegment(sketch, "E14.44.2", {"start": v(-2.46, -25.34) * mm, "end": v(-2.48, -25.52) * mm});
            skArc(sketch, "E14.44.3", {"start": v(-2.46, -25.34) * mm, "mid": v(-2.64, -25.13) * mm, "end": v(-2.86, -25.3) * mm});
            skLineSegment(sketch, "E14.44.4", {"start": v(-2.86, -25.3) * mm, "end": v(-2.88, -25.47) * mm});
            skArc(sketch, "E14.44.5", {"start": v(-3.44, -25.92) * mm, "mid": v(-3.06, -25.8) * mm, "end": v(-2.88, -25.47) * mm});
            skLineSegment(sketch, "E14.44.6", {"start": v(-3.44, -25.92) * mm, "end": v(-3.64, -25.9) * mm});
            skLineSegment(sketch, "E14.45.0", {"start": v(0, -26.15) * mm, "end": v(-0.2, -26.15) * mm});
            skArc(sketch, "E14.45.1", {"start": v(-0.7, -25.63) * mm, "mid": v(-0.55, -25.99) * mm, "end": v(-0.2, -26.15) * mm});
            skLineSegment(sketch, "E14.45.2", {"start": v(-0.69, -25.45) * mm, "end": v(-0.7, -25.63) * mm});
            skArc(sketch, "E14.45.3", {"start": v(-0.69, -25.45) * mm, "mid": v(-0.88, -25.25) * mm, "end": v(-1.09, -25.44) * mm});
            skLineSegment(sketch, "E14.45.4", {"start": v(-1.09, -25.44) * mm, "end": v(-1.1, -25.6) * mm});
            skArc(sketch, "E14.45.5", {"start": v(-1.62, -26.1) * mm, "mid": v(-1.26, -25.96) * mm, "end": v(-1.1, -25.6) * mm});
            skLineSegment(sketch, "E14.45.6", {"start": v(-1.62, -26.1) * mm, "end": v(-1.82, -26.09) * mm});
            skLineSegment(sketch, "E14.46.0", {"start": v(1.82, -26.09) * mm, "end": v(1.62, -26.1) * mm});
            skArc(sketch, "E14.46.1", {"start": v(1.1, -25.61) * mm, "mid": v(1.26, -25.96) * mm, "end": v(1.62, -26.1) * mm});
            skLineSegment(sketch, "E14.46.2", {"start": v(1.09, -25.44) * mm, "end": v(1.1, -25.61) * mm});
            skArc(sketch, "E14.46.3", {"start": v(1.09, -25.44) * mm, "mid": v(0.88, -25.25) * mm, "end": v(0.69, -25.45) * mm});
            skLineSegment(sketch, "E14.46.4", {"start": v(0.69, -25.45) * mm, "end": v(0.7, -25.62) * mm});
            skArc(sketch, "E14.46.5", {"start": v(0.2, -26.15) * mm, "mid": v(0.56, -25.98) * mm, "end": v(0.7, -25.62) * mm});
            skLineSegment(sketch, "E14.46.6", {"start": v(0.2, -26.15) * mm, "end": v(0, -26.15) * mm});
            skLineSegment(sketch, "E14.47.0", {"start": v(3.64, -25.9) * mm, "end": v(3.44, -25.92) * mm});
            skArc(sketch, "E14.47.1", {"start": v(2.88, -25.48) * mm, "mid": v(3.07, -25.81) * mm, "end": v(3.44, -25.92) * mm});
            skLineSegment(sketch, "E14.47.2", {"start": v(2.86, -25.3) * mm, "end": v(2.88, -25.48) * mm});
            skArc(sketch, "E14.47.3", {"start": v(2.86, -25.3) * mm, "mid": v(2.64, -25.13) * mm, "end": v(2.46, -25.34) * mm});
            skLineSegment(sketch, "E14.47.4", {"start": v(2.46, -25.34) * mm, "end": v(2.48, -25.5) * mm});
            skArc(sketch, "E14.47.5", {"start": v(2.03, -26.07) * mm, "mid": v(2.37, -25.88) * mm, "end": v(2.48, -25.5) * mm});
            skLineSegment(sketch, "E14.47.6", {"start": v(2.03, -26.07) * mm, "end": v(1.82, -26.09) * mm});
            skLineSegment(sketch, "E14.48.0", {"start": v(5.44, -25.58) * mm, "end": v(5.24, -25.62) * mm});
            skArc(sketch, "E14.48.1", {"start": v(4.65, -25.21) * mm, "mid": v(4.86, -25.53) * mm, "end": v(5.24, -25.62) * mm});
            skLineSegment(sketch, "E14.48.2", {"start": v(4.62, -25.04) * mm, "end": v(4.65, -25.21) * mm});
            skArc(sketch, "E14.48.3", {"start": v(4.62, -25.04) * mm, "mid": v(4.39, -24.88) * mm, "end": v(4.22, -25.1) * mm});
            skLineSegment(sketch, "E14.48.4", {"start": v(4.22, -25.1) * mm, "end": v(4.25, -25.27) * mm});
            skArc(sketch, "E14.48.5", {"start": v(3.84, -25.86) * mm, "mid": v(4.17, -25.65) * mm, "end": v(4.25, -25.27) * mm});
            skLineSegment(sketch, "E14.48.6", {"start": v(3.84, -25.86) * mm, "end": v(3.64, -25.9) * mm});
            skLineSegment(sketch, "E14.49.0", {"start": v(7.2, -25.14) * mm, "end": v(7.01, -25.19) * mm});
            skArc(sketch, "E14.49.1", {"start": v(6.4, -24.83) * mm, "mid": v(6.63, -25.13) * mm, "end": v(7.01, -25.19) * mm});
            skLineSegment(sketch, "E14.49.2", {"start": v(6.35, -24.66) * mm, "end": v(6.4, -24.83) * mm});
            skArc(sketch, "E14.49.3", {"start": v(6.35, -24.66) * mm, "mid": v(6.11, -24.51) * mm, "end": v(5.97, -24.75) * mm});
            skLineSegment(sketch, "E14.49.4", {"start": v(5.97, -24.75) * mm, "end": v(6, -24.92) * mm});
            skArc(sketch, "E14.49.5", {"start": v(5.64, -25.53) * mm, "mid": v(5.95, -25.3) * mm, "end": v(6, -24.92) * mm});
            skLineSegment(sketch, "E14.49.6", {"start": v(5.64, -25.53) * mm, "end": v(5.44, -25.58) * mm});
            skLineSegment(sketch, "E14.50.0", {"start": v(8.94, -24.58) * mm, "end": v(8.75, -24.64) * mm});
            skArc(sketch, "E14.50.1", {"start": v(8.12, -24.32) * mm, "mid": v(8.37, -24.6) * mm, "end": v(8.75, -24.64) * mm});
            skLineSegment(sketch, "E14.50.2", {"start": v(8.06, -24.15) * mm, "end": v(8.12, -24.32) * mm});
            skArc(sketch, "E14.50.3", {"start": v(8.06, -24.15) * mm, "mid": v(7.8, -24.03) * mm, "end": v(7.68, -24.28) * mm});
            skLineSegment(sketch, "E14.50.4", {"start": v(7.68, -24.28) * mm, "end": v(7.73, -24.44) * mm});
            skArc(sketch, "E14.50.5", {"start": v(7.4, -25.08) * mm, "mid": v(7.7, -24.82) * mm, "end": v(7.73, -24.44) * mm});
            skLineSegment(sketch, "E14.50.6", {"start": v(7.4, -25.08) * mm, "end": v(7.2, -25.14) * mm});
            skLineSegment(sketch, "E14.51.0", {"start": v(10.64, -23.9) * mm, "end": v(10.45, -23.97) * mm});
            skArc(sketch, "E14.51.1", {"start": v(9.8, -23.7) * mm, "mid": v(10.07, -23.97) * mm, "end": v(10.45, -23.97) * mm});
            skLineSegment(sketch, "E14.51.2", {"start": v(9.72, -23.53) * mm, "end": v(9.8, -23.7) * mm});
            skArc(sketch, "E14.51.3", {"start": v(9.72, -23.53) * mm, "mid": v(9.46, -23.42) * mm, "end": v(9.35, -23.68) * mm});
            skLineSegment(sketch, "E14.51.4", {"start": v(9.35, -23.68) * mm, "end": v(9.42, -23.84) * mm});
            skArc(sketch, "E14.51.5", {"start": v(9.13, -24.5) * mm, "mid": v(9.41, -24.23) * mm, "end": v(9.42, -23.84) * mm});
            skLineSegment(sketch, "E14.51.6", {"start": v(9.13, -24.5) * mm, "end": v(8.94, -24.58) * mm});
            skLineSegment(sketch, "E14.52.0", {"start": v(12.28, -23.1) * mm, "end": v(12.1, -23.18) * mm});
            skArc(sketch, "E14.52.1", {"start": v(11.42, -22.95) * mm, "mid": v(11.71, -23.2) * mm, "end": v(12.1, -23.18) * mm});
            skLineSegment(sketch, "E14.52.2", {"start": v(11.34, -22.8) * mm, "end": v(11.42, -22.95) * mm});
            skArc(sketch, "E14.52.3", {"start": v(11.34, -22.8) * mm, "mid": v(11.07, -22.7) * mm, "end": v(10.98, -22.97) * mm});
            skLineSegment(sketch, "E14.52.4", {"start": v(10.98, -22.97) * mm, "end": v(11.06, -23.12) * mm});
            skArc(sketch, "E14.52.5", {"start": v(10.82, -23.8) * mm, "mid": v(11.08, -23.51) * mm, "end": v(11.06, -23.12) * mm});
            skLineSegment(sketch, "E14.52.6", {"start": v(10.82, -23.8) * mm, "end": v(10.64, -23.9) * mm});
            skLineSegment(sketch, "E14.53.0", {"start": v(13.86, -22.18) * mm, "end": v(13.68, -22.28) * mm});
            skArc(sketch, "E14.53.1", {"start": v(13, -22.1) * mm, "mid": v(13.3, -22.33) * mm, "end": v(13.68, -22.28) * mm});
            skLineSegment(sketch, "E14.53.2", {"start": v(12.9, -21.95) * mm, "end": v(13, -22.1) * mm});
            skArc(sketch, "E14.53.3", {"start": v(12.9, -21.95) * mm, "mid": v(12.63, -21.88) * mm, "end": v(12.56, -22.15) * mm});
            skLineSegment(sketch, "E14.53.4", {"start": v(12.56, -22.15) * mm, "end": v(12.64, -22.3) * mm});
            skArc(sketch, "E14.53.5", {"start": v(12.46, -22.99) * mm, "mid": v(12.7, -22.68) * mm, "end": v(12.64, -22.3) * mm});
            skLineSegment(sketch, "E14.53.6", {"start": v(12.46, -22.99) * mm, "end": v(12.28, -23.1) * mm});
            skLineSegment(sketch, "E14.54.0", {"start": v(15.37, -21.16) * mm, "end": v(15.2, -21.27) * mm});
            skArc(sketch, "E14.54.1", {"start": v(14.5, -21.14) * mm, "mid": v(14.83, -21.35) * mm, "end": v(15.2, -21.27) * mm});
            skLineSegment(sketch, "E14.54.2", {"start": v(14.4, -21) * mm, "end": v(14.5, -21.14) * mm});
            skArc(sketch, "E14.54.3", {"start": v(14.4, -21) * mm, "mid": v(14.13, -20.94) * mm, "end": v(14.07, -21.22) * mm});
            skLineSegment(sketch, "E14.54.4", {"start": v(14.07, -21.22) * mm, "end": v(14.17, -21.36) * mm});
            skArc(sketch, "E14.54.5", {"start": v(14.03, -22.06) * mm, "mid": v(14.24, -21.74) * mm, "end": v(14.17, -21.36) * mm});
            skLineSegment(sketch, "E14.54.6", {"start": v(14.03, -22.06) * mm, "end": v(13.86, -22.18) * mm});
            skLineSegment(sketch, "E14.55.0", {"start": v(16.81, -20.03) * mm, "end": v(16.65, -20.16) * mm});
            skArc(sketch, "E14.55.1", {"start": v(15.94, -20.08) * mm, "mid": v(16.28, -20.26) * mm, "end": v(16.65, -20.16) * mm});
            skLineSegment(sketch, "E14.55.2", {"start": v(15.83, -19.94) * mm, "end": v(15.94, -20.08) * mm});
            skArc(sketch, "E14.55.3", {"start": v(15.83, -19.94) * mm, "mid": v(15.55, -19.9) * mm, "end": v(15.52, -20.19) * mm});
            skLineSegment(sketch, "E14.55.4", {"start": v(15.52, -20.19) * mm, "end": v(15.62, -20.32) * mm});
            skArc(sketch, "E14.55.5", {"start": v(15.53, -21.03) * mm, "mid": v(15.72, -20.7) * mm, "end": v(15.62, -20.32) * mm});
            skLineSegment(sketch, "E14.55.6", {"start": v(15.53, -21.03) * mm, "end": v(15.37, -21.16) * mm});
            skLineSegment(sketch, "E14.56.0", {"start": v(18.17, -18.81) * mm, "end": v(18.02, -18.95) * mm});
            skArc(sketch, "E14.56.1", {"start": v(17.3, -18.92) * mm, "mid": v(17.65, -19.08) * mm, "end": v(18.02, -18.95) * mm});
            skLineSegment(sketch, "E14.56.2", {"start": v(17.18, -18.79) * mm, "end": v(17.3, -18.92) * mm});
            skArc(sketch, "E14.56.3", {"start": v(17.18, -18.79) * mm, "mid": v(16.9, -18.77) * mm, "end": v(16.89, -19.05) * mm});
            skLineSegment(sketch, "E14.56.4", {"start": v(16.89, -19.05) * mm, "end": v(17, -19.18) * mm});
            skArc(sketch, "E14.56.5", {"start": v(16.96, -19.9) * mm, "mid": v(17.13, -19.55) * mm, "end": v(17, -19.18) * mm});
            skLineSegment(sketch, "E14.56.6", {"start": v(16.96, -19.9) * mm, "end": v(16.81, -20.03) * mm});
            skLineSegment(sketch, "E14.57.0", {"start": v(19.43, -17.5) * mm, "end": v(19.3, -17.64) * mm});
            skArc(sketch, "E14.57.1", {"start": v(18.58, -17.66) * mm, "mid": v(18.94, -17.8) * mm, "end": v(19.3, -17.64) * mm});
            skLineSegment(sketch, "E14.57.2", {"start": v(18.45, -17.54) * mm, "end": v(18.58, -17.66) * mm});
            skArc(sketch, "E14.57.3", {"start": v(18.45, -17.54) * mm, "mid": v(18.17, -17.55) * mm, "end": v(18.18, -17.83) * mm});
            skLineSegment(sketch, "E14.57.4", {"start": v(18.18, -17.83) * mm, "end": v(18.3, -17.95) * mm});
            skArc(sketch, "E14.57.5", {"start": v(18.3, -18.67) * mm, "mid": v(18.45, -18.3) * mm, "end": v(18.3, -17.95) * mm});
            skLineSegment(sketch, "E14.57.6", {"start": v(18.3, -18.67) * mm, "end": v(18.17, -18.81) * mm});
            skLineSegment(sketch, "E14.58.0", {"start": v(20.6, -16.1) * mm, "end": v(20.48, -16.26) * mm});
            skArc(sketch, "E14.58.1", {"start": v(19.77, -16.32) * mm, "mid": v(20.14, -16.43) * mm, "end": v(20.48, -16.26) * mm});
            skLineSegment(sketch, "E14.58.2", {"start": v(19.63, -16.21) * mm, "end": v(19.77, -16.32) * mm});
            skArc(sketch, "E14.58.3", {"start": v(19.63, -16.21) * mm, "mid": v(19.35, -16.24) * mm, "end": v(19.37, -16.52) * mm});
            skLineSegment(sketch, "E14.58.4", {"start": v(19.37, -16.52) * mm, "end": v(19.5, -16.63) * mm});
            skArc(sketch, "E14.58.5", {"start": v(19.57, -17.34) * mm, "mid": v(19.68, -16.97) * mm, "end": v(19.5, -16.63) * mm});
            skLineSegment(sketch, "E14.58.6", {"start": v(19.57, -17.34) * mm, "end": v(19.43, -17.5) * mm});
            skLineSegment(sketch, "E14.59.0", {"start": v(21.68, -14.62) * mm, "end": v(21.56, -14.79) * mm});
            skArc(sketch, "E14.59.1", {"start": v(20.86, -14.9) * mm, "mid": v(21.24, -14.99) * mm, "end": v(21.56, -14.79) * mm});
            skLineSegment(sketch, "E14.59.2", {"start": v(20.72, -14.8) * mm, "end": v(20.86, -14.9) * mm});
            skArc(sketch, "E14.59.3", {"start": v(20.72, -14.8) * mm, "mid": v(20.44, -14.85) * mm, "end": v(20.48, -15.13) * mm});
            skLineSegment(sketch, "E14.59.4", {"start": v(20.48, -15.13) * mm, "end": v(20.62, -15.23) * mm});
            skArc(sketch, "E14.59.5", {"start": v(20.73, -15.94) * mm, "mid": v(20.82, -15.56) * mm, "end": v(20.62, -15.23) * mm});
            skLineSegment(sketch, "E14.59.6", {"start": v(20.73, -15.94) * mm, "end": v(20.6, -16.1) * mm});
            skLineSegment(sketch, "E14.60.0", {"start": v(22.65, -13.08) * mm, "end": v(22.54, -13.25) * mm});
            skArc(sketch, "E14.60.1", {"start": v(21.85, -13.41) * mm, "mid": v(22.23, -13.47) * mm, "end": v(22.54, -13.25) * mm});
            skLineSegment(sketch, "E14.60.2", {"start": v(21.7, -13.32) * mm, "end": v(21.85, -13.41) * mm});
            skArc(sketch, "E14.60.3", {"start": v(21.7, -13.32) * mm, "mid": v(21.42, -13.39) * mm, "end": v(21.49, -13.66) * mm});
            skLineSegment(sketch, "E14.60.4", {"start": v(21.49, -13.66) * mm, "end": v(21.63, -13.75) * mm});
            skArc(sketch, "E14.60.5", {"start": v(21.79, -14.45) * mm, "mid": v(21.85, -14.07) * mm, "end": v(21.63, -13.75) * mm});
            skLineSegment(sketch, "E14.60.6", {"start": v(21.79, -14.45) * mm, "end": v(21.68, -14.62) * mm});
            skLineSegment(sketch, "E14.61.0", {"start": v(23.5, -11.46) * mm, "end": v(23.41, -11.64) * mm});
            skArc(sketch, "E14.61.1", {"start": v(22.73, -11.86) * mm, "mid": v(23.12, -11.89) * mm, "end": v(23.41, -11.64) * mm});
            skLineSegment(sketch, "E14.61.2", {"start": v(22.57, -11.78) * mm, "end": v(22.73, -11.86) * mm});
            skArc(sketch, "E14.61.3", {"start": v(22.57, -11.78) * mm, "mid": v(22.3, -11.86) * mm, "end": v(22.39, -12.13) * mm});
            skLineSegment(sketch, "E14.61.4", {"start": v(22.39, -12.13) * mm, "end": v(22.53, -12.2) * mm});
            skArc(sketch, "E14.61.5", {"start": v(22.74, -12.9) * mm, "mid": v(22.78, -12.5) * mm, "end": v(22.53, -12.2) * mm});
            skLineSegment(sketch, "E14.61.6", {"start": v(22.74, -12.9) * mm, "end": v(22.65, -13.08) * mm});
            skLineSegment(sketch, "E14.62.0", {"start": v(24.25, -9.8) * mm, "end": v(24.17, -9.98) * mm});
            skArc(sketch, "E14.62.1", {"start": v(23.5, -10.24) * mm, "mid": v(23.89, -10.25) * mm, "end": v(24.17, -9.98) * mm});
            skLineSegment(sketch, "E14.62.2", {"start": v(23.34, -10.17) * mm, "end": v(23.5, -10.24) * mm});
            skArc(sketch, "E14.62.3", {"start": v(23.34, -10.17) * mm, "mid": v(23.08, -10.28) * mm, "end": v(23.18, -10.54) * mm});
            skLineSegment(sketch, "E14.62.4", {"start": v(23.18, -10.54) * mm, "end": v(23.33, -10.6) * mm});
            skArc(sketch, "E14.62.5", {"start": v(23.59, -11.28) * mm, "mid": v(23.6, -10.89) * mm, "end": v(23.33, -10.6) * mm});
            skLineSegment(sketch, "E14.62.6", {"start": v(23.59, -11.28) * mm, "end": v(23.5, -11.46) * mm});
            skLineSegment(sketch, "E14.63.0", {"start": v(24.87, -8.08) * mm, "end": v(24.8, -8.27) * mm});
            skArc(sketch, "E14.63.1", {"start": v(24.16, -8.58) * mm, "mid": v(24.54, -8.56) * mm, "end": v(24.8, -8.27) * mm});
            skLineSegment(sketch, "E14.63.2", {"start": v(24, -8.52) * mm, "end": v(24.16, -8.58) * mm});
            skArc(sketch, "E14.63.3", {"start": v(24, -8.52) * mm, "mid": v(23.74, -8.64) * mm, "end": v(23.86, -8.9) * mm});
            skLineSegment(sketch, "E14.63.4", {"start": v(23.86, -8.9) * mm, "end": v(24.01, -8.95) * mm});
            skArc(sketch, "E14.63.5", {"start": v(24.32, -9.6) * mm, "mid": v(24.3, -9.22) * mm, "end": v(24.01, -8.95) * mm});
            skLineSegment(sketch, "E14.63.6", {"start": v(24.32, -9.6) * mm, "end": v(24.25, -9.8) * mm});
            skLineSegment(sketch, "E14.64.0", {"start": v(25.38, -6.33) * mm, "end": v(25.32, -6.52) * mm});
            skArc(sketch, "E14.64.1", {"start": v(24.7, -6.87) * mm, "mid": v(25.08, -6.82) * mm, "end": v(25.32, -6.52) * mm});
            skLineSegment(sketch, "E14.64.2", {"start": v(24.53, -6.83) * mm, "end": v(24.7, -6.87) * mm});
            skArc(sketch, "E14.64.3", {"start": v(24.53, -6.83) * mm, "mid": v(24.28, -6.96) * mm, "end": v(24.42, -7.2) * mm});
            skLineSegment(sketch, "E14.64.4", {"start": v(24.42, -7.2) * mm, "end": v(24.58, -7.26) * mm});
            skArc(sketch, "E14.64.5", {"start": v(24.93, -7.88) * mm, "mid": v(24.88, -7.5) * mm, "end": v(24.58, -7.26) * mm});
            skLineSegment(sketch, "E14.64.6", {"start": v(24.93, -7.88) * mm, "end": v(24.87, -8.08) * mm});
            skLineSegment(sketch, "E14.65.0", {"start": v(25.75, -4.54) * mm, "end": v(25.71, -4.74) * mm});
            skArc(sketch, "E14.65.1", {"start": v(25.12, -5.13) * mm, "mid": v(25.5, -5.06) * mm, "end": v(25.71, -4.74) * mm});
            skLineSegment(sketch, "E14.65.2", {"start": v(24.95, -5.1) * mm, "end": v(25.12, -5.13) * mm});
            skArc(sketch, "E14.65.3", {"start": v(24.95, -5.1) * mm, "mid": v(24.71, -5.25) * mm, "end": v(24.86, -5.49) * mm});
            skLineSegment(sketch, "E14.65.4", {"start": v(24.86, -5.49) * mm, "end": v(25.03, -5.52) * mm});
            skArc(sketch, "E14.65.5", {"start": v(25.42, -6.13) * mm, "mid": v(25.35, -5.74) * mm, "end": v(25.03, -5.52) * mm});
            skLineSegment(sketch, "E14.65.6", {"start": v(25.42, -6.13) * mm, "end": v(25.38, -6.33) * mm});
            skLineSegment(sketch, "E14.66.0", {"start": v(26, -2.73) * mm, "end": v(25.98, -2.93) * mm});
            skArc(sketch, "E14.66.1", {"start": v(25.42, -3.37) * mm, "mid": v(25.79, -3.27) * mm, "end": v(25.98, -2.93) * mm});
            skLineSegment(sketch, "E14.66.2", {"start": v(25.24, -3.35) * mm, "end": v(25.42, -3.37) * mm});
            skArc(sketch, "E14.66.3", {"start": v(25.24, -3.35) * mm, "mid": v(25.02, -3.52) * mm, "end": v(25.18, -3.74) * mm});
            skLineSegment(sketch, "E14.66.4", {"start": v(25.18, -3.74) * mm, "end": v(25.35, -3.76) * mm});
            skArc(sketch, "E14.66.5", {"start": v(25.78, -4.34) * mm, "mid": v(25.69, -3.96) * mm, "end": v(25.35, -3.76) * mm});
            skLineSegment(sketch, "E14.66.6", {"start": v(25.78, -4.34) * mm, "end": v(25.75, -4.54) * mm});
            skLineSegment(sketch, "E14.67.0", {"start": v(26.14, -0.91) * mm, "end": v(26.12, -1.11) * mm});
            skArc(sketch, "E14.67.1", {"start": v(25.59, -1.59) * mm, "mid": v(25.95, -1.46) * mm, "end": v(26.12, -1.11) * mm});
            skLineSegment(sketch, "E14.67.2", {"start": v(25.41, -1.58) * mm, "end": v(25.59, -1.59) * mm});
            skArc(sketch, "E14.67.3", {"start": v(25.41, -1.58) * mm, "mid": v(25.2, -1.76) * mm, "end": v(25.38, -1.98) * mm});
            skLineSegment(sketch, "E14.67.4", {"start": v(25.38, -1.98) * mm, "end": v(25.55, -1.99) * mm});
            skArc(sketch, "E14.67.5", {"start": v(26.02, -2.53) * mm, "mid": v(25.9, -2.16) * mm, "end": v(25.55, -1.99) * mm});
            skLineSegment(sketch, "E14.67.6", {"start": v(26.02, -2.53) * mm, "end": v(26, -2.73) * mm});
            skLineSegment(sketch, "E14.68.0", {"start": v(26.14, 0.91) * mm, "end": v(26.14, 0.71) * mm});
            skArc(sketch, "E14.68.1", {"start": v(25.64, 0.2) * mm, "mid": v(26, 0.35) * mm, "end": v(26.14, 0.71) * mm});
            skLineSegment(sketch, "E14.68.2", {"start": v(25.46, 0.2) * mm, "end": v(25.64, 0.2) * mm});
            skArc(sketch, "E14.68.3", {"start": v(25.46, 0.2) * mm, "mid": v(25.26, 0) * mm, "end": v(25.46, -0.2) * mm});
            skLineSegment(sketch, "E14.68.4", {"start": v(25.46, -0.2) * mm, "end": v(25.63, -0.2) * mm});
            skArc(sketch, "E14.68.5", {"start": v(26.14, -0.7) * mm, "mid": v(25.99, -0.35) * mm, "end": v(25.63, -0.2) * mm});
            skLineSegment(sketch, "E14.68.6", {"start": v(26.14, -0.7) * mm, "end": v(26.14, -0.91) * mm});
            skLineSegment(sketch, "E14.69.0", {"start": v(26, 2.73) * mm, "end": v(26.02, 2.53) * mm});
            skArc(sketch, "E14.69.1", {"start": v(25.56, 2) * mm, "mid": v(25.9, 2.17) * mm, "end": v(26.02, 2.53) * mm});
            skLineSegment(sketch, "E14.69.2", {"start": v(25.38, 1.98) * mm, "end": v(25.56, 2) * mm});
            skArc(sketch, "E14.69.3", {"start": v(25.38, 1.98) * mm, "mid": v(25.2, 1.76) * mm, "end": v(25.41, 1.58) * mm});
            skLineSegment(sketch, "E14.69.4", {"start": v(25.41, 1.58) * mm, "end": v(25.58, 1.59) * mm});
            skArc(sketch, "E14.69.5", {"start": v(26.12, 1.12) * mm, "mid": v(25.95, 1.46) * mm, "end": v(25.58, 1.59) * mm});
            skLineSegment(sketch, "E14.69.6", {"start": v(26.12, 1.12) * mm, "end": v(26.14, 0.91) * mm});
            skLineSegment(sketch, "E14.70.0", {"start": v(25.75, 4.54) * mm, "end": v(25.78, 4.34) * mm});
            skArc(sketch, "E14.70.1", {"start": v(25.36, 3.77) * mm, "mid": v(25.69, 3.97) * mm, "end": v(25.78, 4.34) * mm});
            skLineSegment(sketch, "E14.70.2", {"start": v(25.18, 3.74) * mm, "end": v(25.36, 3.77) * mm});
            skArc(sketch, "E14.70.3", {"start": v(25.18, 3.74) * mm, "mid": v(25.02, 3.52) * mm, "end": v(25.24, 3.35) * mm});
            skLineSegment(sketch, "E14.70.4", {"start": v(25.24, 3.35) * mm, "end": v(25.4, 3.37) * mm});
            skArc(sketch, "E14.70.5", {"start": v(25.98, 2.94) * mm, "mid": v(25.78, 3.27) * mm, "end": v(25.4, 3.37) * mm});
            skLineSegment(sketch, "E14.70.6", {"start": v(25.98, 2.94) * mm, "end": v(26, 2.73) * mm});
            skLineSegment(sketch, "E14.71.0", {"start": v(25.38, 6.33) * mm, "end": v(25.42, 6.13) * mm});
            skArc(sketch, "E14.71.1", {"start": v(25.03, 5.53) * mm, "mid": v(25.35, 5.75) * mm, "end": v(25.42, 6.13) * mm});
            skLineSegment(sketch, "E14.71.2", {"start": v(24.86, 5.49) * mm, "end": v(25.03, 5.53) * mm});
            skArc(sketch, "E14.71.3", {"start": v(24.86, 5.49) * mm, "mid": v(24.71, 5.25) * mm, "end": v(24.95, 5.1) * mm});
            skLineSegment(sketch, "E14.71.4", {"start": v(24.95, 5.1) * mm, "end": v(25.1, 5.13) * mm});
            skArc(sketch, "E14.71.5", {"start": v(25.71, 4.74) * mm, "mid": v(25.5, 5.06) * mm, "end": v(25.1, 5.13) * mm});
            skLineSegment(sketch, "E14.71.6", {"start": v(25.71, 4.74) * mm, "end": v(25.75, 4.54) * mm});
            skLineSegment(sketch, "E14.72.0", {"start": v(24.87, 8.08) * mm, "end": v(24.93, 7.89) * mm});
            skArc(sketch, "E14.72.1", {"start": v(24.59, 7.26) * mm, "mid": v(24.89, 7.5) * mm, "end": v(24.93, 7.89) * mm});
            skLineSegment(sketch, "E14.72.2", {"start": v(24.42, 7.2) * mm, "end": v(24.59, 7.26) * mm});
            skArc(sketch, "E14.72.3", {"start": v(24.42, 7.2) * mm, "mid": v(24.28, 6.96) * mm, "end": v(24.53, 6.83) * mm});
            skLineSegment(sketch, "E14.72.4", {"start": v(24.53, 6.83) * mm, "end": v(24.7, 6.87) * mm});
            skArc(sketch, "E14.72.5", {"start": v(25.32, 6.52) * mm, "mid": v(25.08, 6.83) * mm, "end": v(24.7, 6.87) * mm});
            skLineSegment(sketch, "E14.72.6", {"start": v(25.32, 6.52) * mm, "end": v(25.38, 6.33) * mm});
            skLineSegment(sketch, "E14.73.0", {"start": v(24.25, 9.8) * mm, "end": v(24.32, 9.6) * mm});
            skArc(sketch, "E14.73.1", {"start": v(24.02, 8.96) * mm, "mid": v(24.3, 9.22) * mm, "end": v(24.32, 9.6) * mm});
            skLineSegment(sketch, "E14.73.2", {"start": v(23.86, 8.9) * mm, "end": v(24.02, 8.96) * mm});
            skArc(sketch, "E14.73.3", {"start": v(23.86, 8.9) * mm, "mid": v(23.74, 8.64) * mm, "end": v(24, 8.52) * mm});
            skLineSegment(sketch, "E14.73.4", {"start": v(24, 8.52) * mm, "end": v(24.15, 8.58) * mm});
            skArc(sketch, "E14.73.5", {"start": v(24.8, 8.27) * mm, "mid": v(24.54, 8.56) * mm, "end": v(24.15, 8.58) * mm});
            skLineSegment(sketch, "E14.73.6", {"start": v(24.8, 8.27) * mm, "end": v(24.87, 8.08) * mm});
            skLineSegment(sketch, "E14.74.0", {"start": v(23.5, 11.46) * mm, "end": v(23.59, 11.28) * mm});
            skArc(sketch, "E14.74.1", {"start": v(23.34, 10.61) * mm, "mid": v(23.6, 10.9) * mm, "end": v(23.59, 11.28) * mm});
            skLineSegment(sketch, "E14.74.2", {"start": v(23.18, 10.54) * mm, "end": v(23.34, 10.61) * mm});
            skArc(sketch, "E14.74.3", {"start": v(23.18, 10.54) * mm, "mid": v(23.08, 10.28) * mm, "end": v(23.34, 10.17) * mm});
            skLineSegment(sketch, "E14.74.4", {"start": v(23.34, 10.17) * mm, "end": v(23.5, 10.24) * mm});
            skArc(sketch, "E14.74.5", {"start": v(24.16, 9.98) * mm, "mid": v(23.88, 10.25) * mm, "end": v(23.5, 10.24) * mm});
            skLineSegment(sketch, "E14.74.6", {"start": v(24.16, 9.98) * mm, "end": v(24.25, 9.8) * mm});
            skLineSegment(sketch, "E14.75.0", {"start": v(22.65, 13.08) * mm, "end": v(22.74, 12.9) * mm});
            skArc(sketch, "E14.75.1", {"start": v(22.54, 12.22) * mm, "mid": v(22.78, 12.52) * mm, "end": v(22.74, 12.9) * mm});
            skLineSegment(sketch, "E14.75.2", {"start": v(22.39, 12.13) * mm, "end": v(22.54, 12.22) * mm});
            skArc(sketch, "E14.75.3", {"start": v(22.39, 12.13) * mm, "mid": v(22.3, 11.86) * mm, "end": v(22.57, 11.78) * mm});
            skLineSegment(sketch, "E14.75.4", {"start": v(22.57, 11.78) * mm, "end": v(22.72, 11.86) * mm});
            skArc(sketch, "E14.75.5", {"start": v(23.4, 11.65) * mm, "mid": v(23.1, 11.9) * mm, "end": v(22.72, 11.86) * mm});
            skLineSegment(sketch, "E14.75.6", {"start": v(23.4, 11.65) * mm, "end": v(23.5, 11.46) * mm});
            skLineSegment(sketch, "E14.76.0", {"start": v(21.68, 14.62) * mm, "end": v(21.79, 14.45) * mm});
            skArc(sketch, "E14.76.1", {"start": v(21.63, 13.76) * mm, "mid": v(21.85, 14.07) * mm, "end": v(21.79, 14.45) * mm});
            skLineSegment(sketch, "E14.76.2", {"start": v(21.49, 13.66) * mm, "end": v(21.63, 13.76) * mm});
            skArc(sketch, "E14.76.3", {"start": v(21.49, 13.66) * mm, "mid": v(21.42, 13.39) * mm, "end": v(21.7, 13.32) * mm});
            skLineSegment(sketch, "E14.76.4", {"start": v(21.7, 13.32) * mm, "end": v(21.84, 13.41) * mm});
            skArc(sketch, "E14.76.5", {"start": v(22.54, 13.25) * mm, "mid": v(22.22, 13.48) * mm, "end": v(21.84, 13.41) * mm});
            skLineSegment(sketch, "E14.76.6", {"start": v(22.54, 13.25) * mm, "end": v(22.65, 13.08) * mm});
            skLineSegment(sketch, "E14.77.0", {"start": v(20.6, 16.1) * mm, "end": v(20.73, 15.94) * mm});
            skArc(sketch, "E14.77.1", {"start": v(20.62, 15.23) * mm, "mid": v(20.82, 15.56) * mm, "end": v(20.73, 15.94) * mm});
            skLineSegment(sketch, "E14.77.2", {"start": v(20.48, 15.13) * mm, "end": v(20.62, 15.23) * mm});
            skArc(sketch, "E14.77.3", {"start": v(20.48, 15.13) * mm, "mid": v(20.44, 14.85) * mm, "end": v(20.72, 14.8) * mm});
            skLineSegment(sketch, "E14.77.4", {"start": v(20.72, 14.8) * mm, "end": v(20.85, 14.9) * mm});
            skArc(sketch, "E14.77.5", {"start": v(21.56, 14.79) * mm, "mid": v(21.23, 15) * mm, "end": v(20.85, 14.9) * mm});
            skLineSegment(sketch, "E14.77.6", {"start": v(21.56, 14.79) * mm, "end": v(21.68, 14.62) * mm});
            skLineSegment(sketch, "E14.78.0", {"start": v(19.43, 17.5) * mm, "end": v(19.56, 17.34) * mm});
            skArc(sketch, "E14.78.1", {"start": v(19.5, 16.63) * mm, "mid": v(19.68, 16.98) * mm, "end": v(19.56, 17.34) * mm});
            skLineSegment(sketch, "E14.78.2", {"start": v(19.37, 16.52) * mm, "end": v(19.5, 16.63) * mm});
            skArc(sketch, "E14.78.3", {"start": v(19.37, 16.52) * mm, "mid": v(19.35, 16.24) * mm, "end": v(19.63, 16.21) * mm});
            skLineSegment(sketch, "E14.78.4", {"start": v(19.63, 16.21) * mm, "end": v(19.76, 16.32) * mm});
            skArc(sketch, "E14.78.5", {"start": v(20.48, 16.26) * mm, "mid": v(20.13, 16.44) * mm, "end": v(19.76, 16.32) * mm});
            skLineSegment(sketch, "E14.78.6", {"start": v(20.48, 16.26) * mm, "end": v(20.6, 16.1) * mm});
            skLineSegment(sketch, "E14.79.0", {"start": v(18.17, 18.81) * mm, "end": v(18.3, 18.67) * mm});
            skArc(sketch, "E14.79.1", {"start": v(18.3, 17.96) * mm, "mid": v(18.45, 18.3) * mm, "end": v(18.3, 18.67) * mm});
            skLineSegment(sketch, "E14.79.2", {"start": v(18.18, 17.83) * mm, "end": v(18.3, 17.96) * mm});
            skArc(sketch, "E14.79.3", {"start": v(18.18, 17.83) * mm, "mid": v(18.17, 17.55) * mm, "end": v(18.45, 17.54) * mm});
            skLineSegment(sketch, "E14.79.4", {"start": v(18.45, 17.54) * mm, "end": v(18.57, 17.66) * mm});
            skArc(sketch, "E14.79.5", {"start": v(19.3, 17.65) * mm, "mid": v(18.94, 17.8) * mm, "end": v(18.57, 17.66) * mm});
            skLineSegment(sketch, "E14.79.6", {"start": v(19.3, 17.65) * mm, "end": v(19.43, 17.5) * mm});
            skLineSegment(sketch, "E14.80.0", {"start": v(16.81, 20.03) * mm, "end": v(16.96, 19.9) * mm});
            skArc(sketch, "E14.80.1", {"start": v(17, 19.19) * mm, "mid": v(17.13, 19.55) * mm, "end": v(16.96, 19.9) * mm});
            skLineSegment(sketch, "E14.80.2", {"start": v(16.89, 19.05) * mm, "end": v(17, 19.19) * mm});
            skArc(sketch, "E14.80.3", {"start": v(16.89, 19.05) * mm, "mid": v(16.9, 18.77) * mm, "end": v(17.18, 18.79) * mm});
            skLineSegment(sketch, "E14.80.4", {"start": v(17.18, 18.79) * mm, "end": v(17.3, 18.91) * mm});
            skArc(sketch, "E14.80.5", {"start": v(18.01, 18.95) * mm, "mid": v(17.65, 19.08) * mm, "end": v(17.3, 18.91) * mm});
            skLineSegment(sketch, "E14.80.6", {"start": v(18.01, 18.95) * mm, "end": v(18.17, 18.81) * mm});
            skLineSegment(sketch, "E14.81.0", {"start": v(15.37, 21.16) * mm, "end": v(15.53, 21.03) * mm});
            skArc(sketch, "E14.81.1", {"start": v(15.62, 20.33) * mm, "mid": v(15.72, 20.7) * mm, "end": v(15.53, 21.03) * mm});
            skLineSegment(sketch, "E14.81.2", {"start": v(15.52, 20.19) * mm, "end": v(15.62, 20.33) * mm});
            skArc(sketch, "E14.81.3", {"start": v(15.52, 20.19) * mm, "mid": v(15.55, 19.9) * mm, "end": v(15.83, 19.94) * mm});
            skLineSegment(sketch, "E14.81.4", {"start": v(15.83, 19.94) * mm, "end": v(15.94, 20.07) * mm});
            skArc(sketch, "E14.81.5", {"start": v(16.65, 20.16) * mm, "mid": v(16.27, 20.26) * mm, "end": v(15.94, 20.07) * mm});
            skLineSegment(sketch, "E14.81.6", {"start": v(16.65, 20.16) * mm, "end": v(16.81, 20.03) * mm});
            skLineSegment(sketch, "E14.82.0", {"start": v(13.86, 22.18) * mm, "end": v(14.03, 22.07) * mm});
            skArc(sketch, "E14.82.1", {"start": v(14.17, 21.37) * mm, "mid": v(14.24, 21.75) * mm, "end": v(14.03, 22.07) * mm});
            skLineSegment(sketch, "E14.82.2", {"start": v(14.07, 21.22) * mm, "end": v(14.17, 21.37) * mm});
            skArc(sketch, "E14.82.3", {"start": v(14.07, 21.22) * mm, "mid": v(14.13, 20.94) * mm, "end": v(14.4, 21) * mm});
            skLineSegment(sketch, "E14.82.4", {"start": v(14.4, 21) * mm, "end": v(14.5, 21.14) * mm});
            skArc(sketch, "E14.82.5", {"start": v(15.2, 21.27) * mm, "mid": v(14.82, 21.35) * mm, "end": v(14.5, 21.14) * mm});
            skLineSegment(sketch, "E14.82.6", {"start": v(15.2, 21.27) * mm, "end": v(15.37, 21.16) * mm});
            skLineSegment(sketch, "E14.83.0", {"start": v(12.28, 23.1) * mm, "end": v(12.45, 23) * mm});
            skArc(sketch, "E14.83.1", {"start": v(12.64, 22.3) * mm, "mid": v(12.69, 22.69) * mm, "end": v(12.45, 23) * mm});
            skLineSegment(sketch, "E14.83.2", {"start": v(12.56, 22.15) * mm, "end": v(12.64, 22.3) * mm});
            skArc(sketch, "E14.83.3", {"start": v(12.56, 22.15) * mm, "mid": v(12.63, 21.88) * mm, "end": v(12.9, 21.95) * mm});
            skLineSegment(sketch, "E14.83.4", {"start": v(12.9, 21.95) * mm, "end": v(12.99, 22.1) * mm});
            skArc(sketch, "E14.83.5", {"start": v(13.68, 22.28) * mm, "mid": v(13.3, 22.33) * mm, "end": v(12.99, 22.1) * mm});
            skLineSegment(sketch, "E14.83.6", {"start": v(13.68, 22.28) * mm, "end": v(13.86, 22.18) * mm});
            skLineSegment(sketch, "E14.84.0", {"start": v(10.64, 23.9) * mm, "end": v(10.82, 23.8) * mm});
            skArc(sketch, "E14.84.1", {"start": v(11.06, 23.13) * mm, "mid": v(11.07, 23.52) * mm, "end": v(10.82, 23.8) * mm});
            skLineSegment(sketch, "E14.84.2", {"start": v(10.98, 22.97) * mm, "end": v(11.06, 23.13) * mm});
            skArc(sketch, "E14.84.3", {"start": v(10.98, 22.97) * mm, "mid": v(11.07, 22.7) * mm, "end": v(11.34, 22.8) * mm});
            skLineSegment(sketch, "E14.84.4", {"start": v(11.34, 22.8) * mm, "end": v(11.41, 22.95) * mm});
            skArc(sketch, "E14.84.5", {"start": v(12.1, 23.18) * mm, "mid": v(11.7, 23.2) * mm, "end": v(11.41, 22.95) * mm});
            skLineSegment(sketch, "E14.84.6", {"start": v(12.1, 23.18) * mm, "end": v(12.28, 23.1) * mm});
            skLineSegment(sketch, "E14.85.0", {"start": v(8.94, 24.58) * mm, "end": v(9.13, 24.5) * mm});
            skArc(sketch, "E14.85.1", {"start": v(9.42, 23.85) * mm, "mid": v(9.4, 24.23) * mm, "end": v(9.13, 24.5) * mm});
            skLineSegment(sketch, "E14.85.2", {"start": v(9.35, 23.68) * mm, "end": v(9.42, 23.85) * mm});
            skArc(sketch, "E14.85.3", {"start": v(9.35, 23.68) * mm, "mid": v(9.46, 23.42) * mm, "end": v(9.72, 23.53) * mm});
            skLineSegment(sketch, "E14.85.4", {"start": v(9.72, 23.53) * mm, "end": v(9.79, 23.69) * mm});
            skArc(sketch, "E14.85.5", {"start": v(10.45, 23.97) * mm, "mid": v(10.06, 23.96) * mm, "end": v(9.79, 23.69) * mm});
            skLineSegment(sketch, "E14.85.6", {"start": v(10.45, 23.97) * mm, "end": v(10.64, 23.9) * mm});
            skLineSegment(sketch, "E14.86.0", {"start": v(7.2, 25.14) * mm, "end": v(7.4, 25.08) * mm});
            skArc(sketch, "E14.86.1", {"start": v(7.73, 24.45) * mm, "mid": v(7.7, 24.83) * mm, "end": v(7.4, 25.08) * mm});
            skLineSegment(sketch, "E14.86.2", {"start": v(7.68, 24.28) * mm, "end": v(7.73, 24.45) * mm});
            skArc(sketch, "E14.86.3", {"start": v(7.68, 24.28) * mm, "mid": v(7.8, 24.03) * mm, "end": v(8.06, 24.15) * mm});
            skLineSegment(sketch, "E14.86.4", {"start": v(8.06, 24.15) * mm, "end": v(8.1, 24.31) * mm});
            skArc(sketch, "E14.86.5", {"start": v(8.75, 24.64) * mm, "mid": v(8.36, 24.6) * mm, "end": v(8.1, 24.31) * mm});
            skLineSegment(sketch, "E14.86.6", {"start": v(8.75, 24.64) * mm, "end": v(8.94, 24.58) * mm});
            skLineSegment(sketch, "E14.87.0", {"start": v(5.44, 25.58) * mm, "end": v(5.63, 25.53) * mm});
            skArc(sketch, "E14.87.1", {"start": v(6, 24.92) * mm, "mid": v(5.94, 25.3) * mm, "end": v(5.63, 25.53) * mm});
            skLineSegment(sketch, "E14.87.2", {"start": v(5.97, 24.75) * mm, "end": v(6, 24.92) * mm});
            skArc(sketch, "E14.87.3", {"start": v(5.97, 24.75) * mm, "mid": v(6.11, 24.51) * mm, "end": v(6.35, 24.66) * mm});
            skLineSegment(sketch, "E14.87.4", {"start": v(6.35, 24.66) * mm, "end": v(6.4, 24.82) * mm});
            skArc(sketch, "E14.87.5", {"start": v(7, 25.19) * mm, "mid": v(6.63, 25.13) * mm, "end": v(6.4, 24.82) * mm});
            skLineSegment(sketch, "E14.87.6", {"start": v(7, 25.19) * mm, "end": v(7.2, 25.14) * mm});
            skLineSegment(sketch, "E14.88.0", {"start": v(3.64, 25.9) * mm, "end": v(3.84, 25.86) * mm});
            skArc(sketch, "E14.88.1", {"start": v(4.25, 25.28) * mm, "mid": v(4.16, 25.66) * mm, "end": v(3.84, 25.86) * mm});
            skLineSegment(sketch, "E14.88.2", {"start": v(4.22, 25.1) * mm, "end": v(4.25, 25.28) * mm});
            skArc(sketch, "E14.88.3", {"start": v(4.22, 25.1) * mm, "mid": v(4.39, 24.88) * mm, "end": v(4.62, 25.04) * mm});
            skLineSegment(sketch, "E14.88.4", {"start": v(4.62, 25.04) * mm, "end": v(4.65, 25.2) * mm});
            skArc(sketch, "E14.88.5", {"start": v(5.24, 25.62) * mm, "mid": v(4.86, 25.53) * mm, "end": v(4.65, 25.2) * mm});
            skLineSegment(sketch, "E14.88.6", {"start": v(5.24, 25.62) * mm, "end": v(5.44, 25.58) * mm});
            skLineSegment(sketch, "E14.89.0", {"start": v(1.82, 26.09) * mm, "end": v(2.02, 26.07) * mm});
            skArc(sketch, "E14.89.1", {"start": v(2.48, 25.52) * mm, "mid": v(2.36, 25.89) * mm, "end": v(2.02, 26.07) * mm});
            skLineSegment(sketch, "E14.89.2", {"start": v(2.46, 25.34) * mm, "end": v(2.48, 25.52) * mm});
            skArc(sketch, "E14.89.3", {"start": v(2.46, 25.34) * mm, "mid": v(2.64, 25.13) * mm, "end": v(2.86, 25.3) * mm});
            skLineSegment(sketch, "E14.89.4", {"start": v(2.86, 25.3) * mm, "end": v(2.88, 25.47) * mm});
            skArc(sketch, "E14.89.5", {"start": v(3.44, 25.92) * mm, "mid": v(3.06, 25.8) * mm, "end": v(2.88, 25.47) * mm});
            skLineSegment(sketch, "E14.89.6", {"start": v(3.44, 25.92) * mm, "end": v(3.64, 25.9) * mm});
            skPoint(sketch, "E14.center", {"position": v(0, 0) * mm});
            skCircle(sketch, "E15", {"center": v(0, 0) * mm, "radius": 19.3 * mm});
            skSolve(sketch);
        }
        {
            var Q0;
            Q0 = qSketchRegion(id + "F0", true);
            extrude(context, id + "F1", {"entities" : qUnion([Q0]), "depth" : 3.17 * mm, "offsetDistance" : 25.4 * mm});
        }
    });
